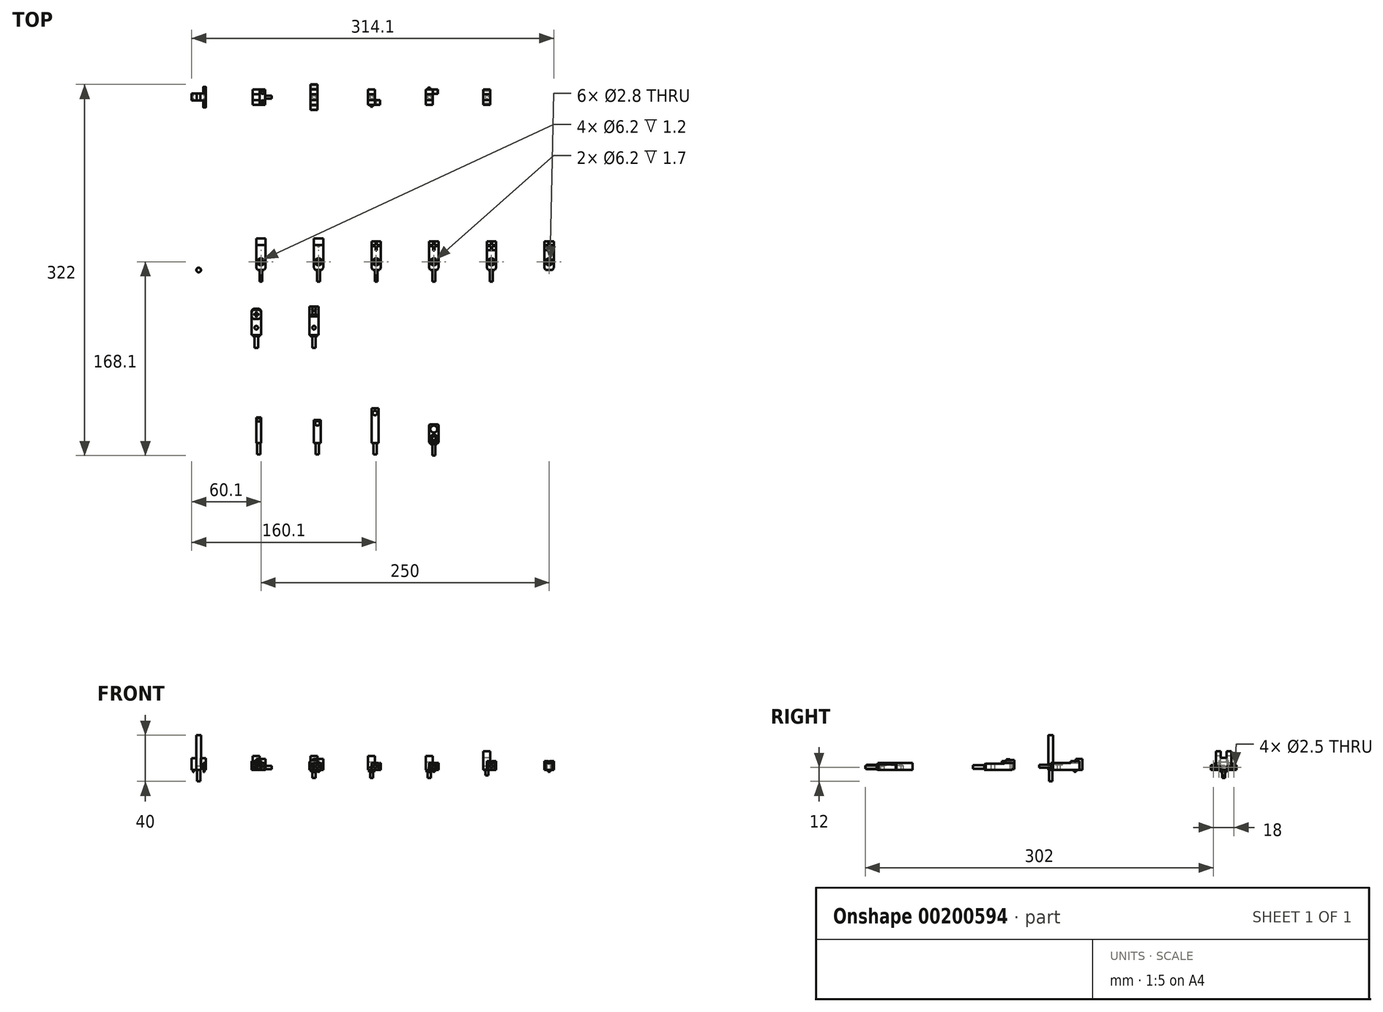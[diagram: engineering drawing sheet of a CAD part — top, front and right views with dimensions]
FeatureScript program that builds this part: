
annotation { "Feature Type Name" : "Feature", "Feature Type Description" : "" }
export const myFeature = defineFeature(function(context is Context, id is Id, definition is map)
    precondition{}
    {
        {
            var Q0;
            Q0=qCreatedBy(makeId("Top.planeOp"),FACE);
            var sketch = newSketch(context, id + "F0", { "sketchPlane" : qUnion([Q0])});
            skPoint(sketch, "E0", {"position": v(0, 0) * mm});
            skPoint(sketch, "E1.0.1.0", {"position": v(0, -50) * mm});
            skPoint(sketch, "E1.0.2.0", {"position": v(0, -100) * mm});
            skPoint(sketch, "E1.0.3.0", {"position": v(0, -150) * mm});
            skPoint(sketch, "E1.0.4.0", {"position": v(0, -200) * mm});
            skPoint(sketch, "E1.0.5.0", {"position": v(0, -250) * mm});
            skPoint(sketch, "E1.0.6.0", {"position": v(0, -300) * mm});
            skPoint(sketch, "E1.0.7.0", {"position": v(0, -350) * mm});
            skPoint(sketch, "E1.0.8.0", {"position": v(0, -400) * mm});
            skPoint(sketch, "E1.0.9.0", {"position": v(0, -450) * mm});
            skPoint(sketch, "E1.1.0.0", {"position": v(50, 0) * mm});
            skPoint(sketch, "E1.1.1.0", {"position": v(50, -50) * mm});
            skPoint(sketch, "E1.1.2.0", {"position": v(50, -100) * mm});
            skPoint(sketch, "E1.1.3.0", {"position": v(50, -150) * mm});
            skPoint(sketch, "E1.1.4.0", {"position": v(50, -200) * mm});
            skPoint(sketch, "E1.1.5.0", {"position": v(50, -250) * mm});
            skPoint(sketch, "E1.1.6.0", {"position": v(50, -300) * mm});
            skPoint(sketch, "E1.1.7.0", {"position": v(50, -350) * mm});
            skPoint(sketch, "E1.1.8.0", {"position": v(50, -400) * mm});
            skPoint(sketch, "E1.1.9.0", {"position": v(50, -450) * mm});
            skPoint(sketch, "E1.2.0.0", {"position": v(100, 0) * mm});
            skPoint(sketch, "E1.2.1.0", {"position": v(100, -50) * mm});
            skPoint(sketch, "E1.2.2.0", {"position": v(100, -100) * mm});
            skPoint(sketch, "E1.2.3.0", {"position": v(100, -150) * mm});
            skPoint(sketch, "E1.2.4.0", {"position": v(100, -200) * mm});
            skPoint(sketch, "E1.2.5.0", {"position": v(100, -250) * mm});
            skPoint(sketch, "E1.2.6.0", {"position": v(100, -300) * mm});
            skPoint(sketch, "E1.2.7.0", {"position": v(100, -350) * mm});
            skPoint(sketch, "E1.2.8.0", {"position": v(100, -400) * mm});
            skPoint(sketch, "E1.2.9.0", {"position": v(100, -450) * mm});
            skPoint(sketch, "E1.3.0.0", {"position": v(150, 0) * mm});
            skPoint(sketch, "E1.3.1.0", {"position": v(150, -50) * mm});
            skPoint(sketch, "E1.3.2.0", {"position": v(150, -100) * mm});
            skPoint(sketch, "E1.3.3.0", {"position": v(150, -150) * mm});
            skPoint(sketch, "E1.3.4.0", {"position": v(150, -200) * mm});
            skPoint(sketch, "E1.3.5.0", {"position": v(150, -250) * mm});
            skPoint(sketch, "E1.3.6.0", {"position": v(150, -300) * mm});
            skPoint(sketch, "E1.3.7.0", {"position": v(150, -350) * mm});
            skPoint(sketch, "E1.3.8.0", {"position": v(150, -400) * mm});
            skPoint(sketch, "E1.3.9.0", {"position": v(150, -450) * mm});
            skPoint(sketch, "E1.4.0.0", {"position": v(200, 0) * mm});
            skPoint(sketch, "E1.4.1.0", {"position": v(200, -50) * mm});
            skPoint(sketch, "E1.4.2.0", {"position": v(200, -100) * mm});
            skPoint(sketch, "E1.4.3.0", {"position": v(200, -150) * mm});
            skPoint(sketch, "E1.4.4.0", {"position": v(200, -200) * mm});
            skPoint(sketch, "E1.4.5.0", {"position": v(200, -250) * mm});
            skPoint(sketch, "E1.4.6.0", {"position": v(200, -300) * mm});
            skPoint(sketch, "E1.4.7.0", {"position": v(200, -350) * mm});
            skPoint(sketch, "E1.4.8.0", {"position": v(200, -400) * mm});
            skPoint(sketch, "E1.4.9.0", {"position": v(200, -450) * mm});
            skPoint(sketch, "E1.5.0.0", {"position": v(250, 0) * mm});
            skPoint(sketch, "E1.5.1.0", {"position": v(250, -50) * mm});
            skPoint(sketch, "E1.5.2.0", {"position": v(250, -100) * mm});
            skPoint(sketch, "E1.5.3.0", {"position": v(250, -150) * mm});
            skPoint(sketch, "E1.5.4.0", {"position": v(250, -200) * mm});
            skPoint(sketch, "E1.5.5.0", {"position": v(250, -250) * mm});
            skPoint(sketch, "E1.5.6.0", {"position": v(250, -300) * mm});
            skPoint(sketch, "E1.5.7.0", {"position": v(250, -350) * mm});
            skPoint(sketch, "E1.5.8.0", {"position": v(250, -400) * mm});
            skPoint(sketch, "E1.5.9.0", {"position": v(250, -450) * mm});
            skPoint(sketch, "E1.6.0.0", {"position": v(300, 0) * mm});
            skPoint(sketch, "E1.6.1.0", {"position": v(300, -50) * mm});
            skPoint(sketch, "E1.6.2.0", {"position": v(300, -100) * mm});
            skPoint(sketch, "E1.6.3.0", {"position": v(300, -150) * mm});
            skPoint(sketch, "E1.6.4.0", {"position": v(300, -200) * mm});
            skPoint(sketch, "E1.6.5.0", {"position": v(300, -250) * mm});
            skPoint(sketch, "E1.6.6.0", {"position": v(300, -300) * mm});
            skPoint(sketch, "E1.6.7.0", {"position": v(300, -350) * mm});
            skPoint(sketch, "E1.6.8.0", {"position": v(300, -400) * mm});
            skPoint(sketch, "E1.6.9.0", {"position": v(300, -450) * mm});
            skPoint(sketch, "E1.7.0.0", {"position": v(350, 0) * mm});
            skPoint(sketch, "E1.7.1.0", {"position": v(350, -50) * mm});
            skPoint(sketch, "E1.7.2.0", {"position": v(350, -100) * mm});
            skPoint(sketch, "E1.7.3.0", {"position": v(350, -150) * mm});
            skPoint(sketch, "E1.7.4.0", {"position": v(350, -200) * mm});
            skPoint(sketch, "E1.7.5.0", {"position": v(350, -250) * mm});
            skPoint(sketch, "E1.7.6.0", {"position": v(350, -300) * mm});
            skPoint(sketch, "E1.7.7.0", {"position": v(350, -350) * mm});
            skPoint(sketch, "E1.7.8.0", {"position": v(350, -400) * mm});
            skPoint(sketch, "E1.7.9.0", {"position": v(350, -450) * mm});
            skPoint(sketch, "E1.8.0.0", {"position": v(400, 0) * mm});
            skPoint(sketch, "E1.8.1.0", {"position": v(400, -50) * mm});
            skPoint(sketch, "E1.8.2.0", {"position": v(400, -100) * mm});
            skPoint(sketch, "E1.8.3.0", {"position": v(400, -150) * mm});
            skPoint(sketch, "E1.8.4.0", {"position": v(400, -200) * mm});
            skPoint(sketch, "E1.8.5.0", {"position": v(400, -250) * mm});
            skPoint(sketch, "E1.8.6.0", {"position": v(400, -300) * mm});
            skPoint(sketch, "E1.8.7.0", {"position": v(400, -350) * mm});
            skPoint(sketch, "E1.8.8.0", {"position": v(400, -400) * mm});
            skPoint(sketch, "E1.8.9.0", {"position": v(400, -450) * mm});
            skPoint(sketch, "E1.9.0.0", {"position": v(450, 0) * mm});
            skPoint(sketch, "E1.9.1.0", {"position": v(450, -50) * mm});
            skPoint(sketch, "E1.9.2.0", {"position": v(450, -100) * mm});
            skPoint(sketch, "E1.9.3.0", {"position": v(450, -150) * mm});
            skPoint(sketch, "E1.9.4.0", {"position": v(450, -200) * mm});
            skPoint(sketch, "E1.9.5.0", {"position": v(450, -250) * mm});
            skPoint(sketch, "E1.9.6.0", {"position": v(450, -300) * mm});
            skPoint(sketch, "E1.9.7.0", {"position": v(450, -350) * mm});
            skPoint(sketch, "E1.9.8.0", {"position": v(450, -400) * mm});
            skPoint(sketch, "E1.9.9.0", {"position": v(450, -450) * mm});
            skLineSegment(sketch, "E1.direction1", {"start": v(0, 0) * mm, "end": v(50, 0) * mm, "construction": true});
            skLineSegment(sketch, "E1.direction2", {"start": v(0, 0) * mm, "end": v(0, -50) * mm, "construction": true});
            skSolve(sketch);
        }
        {
            var Q0;
            Q0=qCreatedBy(makeId("Top.planeOp"),FACE);
            var sketch = newSketch(context, id + "F1", { "sketchPlane" : qUnion([Q0])});
            skLineSegment(sketch, "E2.bottom", {"start": v(6.1, 3) * mm, "end": v(-6.1, 3) * mm});
            skLineSegment(sketch, "E2.top", {"start": v(6.1, -3) * mm, "end": v(-6.1, -3) * mm});
            skLineSegment(sketch, "E2.left", {"start": v(6.1, 3) * mm, "end": v(6.1, -3) * mm});
            skLineSegment(sketch, "E2.right", {"start": v(-6.1, 3) * mm, "end": v(-6.1, -3) * mm});
            skPoint(sketch, "E2.middle", {"position": v(0, 0) * mm});
            skSolve(sketch);
        }
        {
            var Q0;
            Q0 = qSketchRegion(id + "F1", true);
            extrude(context, id + "F2", {"entities" : qUnion([Q0]), "depth" : 10 * mm});
        }
        {
            var Q0;
            Q0=makeQuery(id+"F2.opExtrude","SWEPT_FACE",FACE,{"disambiguationData":[OSD([sQuery(id+"F1.wireOp",EDGE,"E2.left")])]});
            var sketch = newSketch(context, id + "F3", { "sketchPlane" : qUnion([Q0])});
            skLineSegment(sketch, "E3.bottom", {"start": v(6, 6) * mm, "end": v(-6, 6) * mm});
            skLineSegment(sketch, "E3.top", {"start": v(6, 0) * mm, "end": v(-6, 0) * mm});
            skPoint(sketch, "E3.middle", {"position": v(0, 3) * mm});
            skPoint(sketch, "E3.middle.positionSnap0", {"position": v(0, 0) * mm});
            skPoint(sketch, "E3.centerSnap0", {"position": v(0, 0) * mm});
            skArc(sketch, "E4", {"start": v(-6, 6) * mm, "mid": v(-9, 3) * mm, "end": v(-6, 0) * mm});
            skArc(sketch, "E5", {"start": v(6, 0) * mm, "mid": v(9, 3) * mm, "end": v(6, 6) * mm});
            skSolve(sketch);
        }
        {
            var Q0;
            Q0 = qSketchRegion(id + "F3", true);
            extrude(context, id + "F4", {"entities" : qUnion([Q0]), "operationType" : NewBodyOperationType.ADD, "oppositeDirection" : true, "depth" : 2 * mm});
        }
        {
            var Q0;
            Q0=makeQuery(id+"F4.boolean.opBoolean","MERGE",FACE,{"derivedFrom":[makeQuery(id+"F2.opExtrude","SWEPT_FACE",FACE,{"disambiguationData":[OSD([sQuery(id+"F1.wireOp",EDGE,"E2.left")])]}),makeQuery(id+"F4.opExtrude","CAP_FACE",FACE,{"disambiguationData":[OSD([sQuery(id+"F3.wireOp",EDGE,"E3.bottom"),sQuery(id+"F3.wireOp",EDGE,"E3.top"),sQuery(id+"F3.wireOp",EDGE,"E4"),sQuery(id+"F3.wireOp",EDGE,"E5")])],"isStart":true})]});
            var sketch = newSketch(context, id + "F5", { "sketchPlane" : qUnion([Q0])});
            skCircle(sketch, "E6", {"center": v(-6, 3) * mm, "radius": 1.6 * mm});
            skCircle(sketch, "E7", {"center": v(6, 3) * mm, "radius": 1.6 * mm});
            skSolve(sketch);
        }
        {
            var Q0;
            Q0 = qSketchRegion(id + "F5", true);
            extrude(context, id + "F6", {"entities" : qUnion([Q0]), "operationType" : NewBodyOperationType.REMOVE, "endBound" : BoundingType.UP_TO_NEXT, "oppositeDirection" : true, "depth" : 25 * mm});
        }
        {
            var Q0;
            Q0=makeQuery(id+"F2.opExtrude","CAP_FACE",FACE,{"disambiguationData":[OSD([sQuery(id+"F1.wireOp",EDGE,"E2.bottom"),sQuery(id+"F1.wireOp",EDGE,"E2.top"),sQuery(id+"F1.wireOp",EDGE,"E2.left"),sQuery(id+"F1.wireOp",EDGE,"E2.right")])],"isStart":false});
            var sketch = newSketch(context, id + "F7", { "sketchPlane" : qUnion([Q0])});
            skLineSegment(sketch, "E8.bottom", {"start": v(1.6, 3) * mm, "end": v(-1.6, 3) * mm});
            skLineSegment(sketch, "E8.top", {"start": v(1.6, -3) * mm, "end": v(-1.6, -3) * mm});
            skLineSegment(sketch, "E8.left", {"start": v(1.6, 3) * mm, "end": v(1.6, -3) * mm});
            skLineSegment(sketch, "E8.right", {"start": v(-1.6, 3) * mm, "end": v(-1.6, -3) * mm});
            skPoint(sketch, "E8.middle", {"position": v(0, 0) * mm});
            skSolve(sketch);
        }
        {
            var Q0;
            Q0 = qSketchRegion(id + "F7", true);
            extrude(context, id + "F8", {"entities" : qUnion([Q0]), "operationType" : NewBodyOperationType.REMOVE, "oppositeDirection" : true, "depth" : 7 * mm});
        }
        {
            var Q0;
            Q0=makeQuery(id+"F4.boolean.opBoolean","MERGE",FACE,{"derivedFrom":[makeQuery(id+"F2.opExtrude","CAP_FACE",FACE,{"disambiguationData":[OSD([sQuery(id+"F1.wireOp",EDGE,"E2.bottom"),sQuery(id+"F1.wireOp",EDGE,"E2.top"),sQuery(id+"F1.wireOp",EDGE,"E2.left"),sQuery(id+"F1.wireOp",EDGE,"E2.right")])],"isStart":true}),makeQuery(id+"F4.opExtrude","SWEPT_FACE",FACE,{"disambiguationData":[OSD([sQuery(id+"F3.wireOp",EDGE,"E3.top")])]})]});
            var sketch = newSketch(context, id + "F9", { "sketchPlane" : qUnion([Q0])});
            skLineSegment(sketch, "E9.bottom", {"start": v(4.6, 1.27) * mm, "end": v(-4.6, 1.27) * mm, "construction": true});
            skLineSegment(sketch, "E9.top", {"start": v(4.6, -1.27) * mm, "end": v(-4.6, -1.27) * mm, "construction": true});
            skLineSegment(sketch, "E9.left", {"start": v(4.6, 1.27) * mm, "end": v(4.6, -1.27) * mm, "construction": true});
            skLineSegment(sketch, "E9.right", {"start": v(-4.6, 1.27) * mm, "end": v(-4.6, -1.27) * mm, "construction": true});
            skPoint(sketch, "E9.middle", {"position": v(0, 0) * mm});
            skCircle(sketch, "E10", {"center": v(-4.6, 1.27) * mm, "radius": 0.23 * mm});
            skCircle(sketch, "E11", {"center": v(4.6, 1.27) * mm, "radius": 0.23 * mm});
            skCircle(sketch, "E12", {"center": v(4.6, -1.27) * mm, "radius": 0.23 * mm});
            skCircle(sketch, "E13", {"center": v(-4.6, -1.27) * mm, "radius": 0.23 * mm});
            skSolve(sketch);
        }
        {
            var Q0;
            Q0 = qSketchRegion(id + "F9", true);
            extrude(context, id + "F10", {"entities" : qUnion([Q0]), "operationType" : NewBodyOperationType.ADD, "depth" : 2 * mm});
        }
        {
            var Q0;
            Q0=qCreatedBy(makeId("Top.planeOp"),FACE);
            var sketch = newSketch(context, id + "F11", { "sketchPlane" : qUnion([Q0])});
            skLineSegment(sketch, "E14.bottom", {"start": v(53, 6.7) * mm, "end": v(47, 6.7) * mm});
            skLineSegment(sketch, "E14.top", {"start": v(53, -6.7) * mm, "end": v(47, -6.7) * mm});
            skLineSegment(sketch, "E14.left", {"start": v(53, 6.7) * mm, "end": v(53, -6.7) * mm});
            skLineSegment(sketch, "E14.right", {"start": v(47, 6.7) * mm, "end": v(47, -6.7) * mm});
            skPoint(sketch, "E14.middle", {"position": v(50, 0) * mm});
            skSolve(sketch);
        }
        {
            var Q0;
            Q0 = qSketchRegion(id + "F11", true);
            extrude(context, id + "F12", {"entities" : qUnion([Q0]), "depth" : 12 * mm});
        }
        {
            var Q0;
            Q0=makeQuery(id+"F12.opExtrude","CAP_FACE",FACE,{"disambiguationData":[OSD([sQuery(id+"F11.wireOp",EDGE,"E14.bottom"),sQuery(id+"F11.wireOp",EDGE,"E14.top"),sQuery(id+"F11.wireOp",EDGE,"E14.left"),sQuery(id+"F11.wireOp",EDGE,"E14.right")])],"isStart":false});
            var sketch = newSketch(context, id + "F13", { "sketchPlane" : qUnion([Q0])});
            skLineSegment(sketch, "E15.bottom", {"start": v(53, 2.5) * mm, "end": v(47, 2.5) * mm});
            skLineSegment(sketch, "E15.top", {"start": v(53, -2.5) * mm, "end": v(47, -2.5) * mm});
            skLineSegment(sketch, "E15.left", {"start": v(53, 2.5) * mm, "end": v(53, -2.5) * mm});
            skLineSegment(sketch, "E15.right", {"start": v(47, 2.5) * mm, "end": v(47, -2.5) * mm});
            skPoint(sketch, "E15.middle", {"position": v(50, 0) * mm});
            skPoint(sketch, "E15.middle.positionSnap0", {"position": v(50, 6.7) * mm});
            skPoint(sketch, "E15.middle.positionSnap1", {"position": v(47, 0) * mm});
            skPoint(sketch, "E15.centerSnap0", {"position": v(50, 6.7) * mm});
            skPoint(sketch, "E15.centerSnap1", {"position": v(47, 0) * mm});
            skSolve(sketch);
        }
        {
            var Q0;
            Q0 = qSketchRegion(id + "F13", true);
            extrude(context, id + "F14", {"entities" : qUnion([Q0]), "operationType" : NewBodyOperationType.REMOVE, "oppositeDirection" : true, "depth" : 5.5 * mm});
        }
        {
            var Q0;
            Q0=makeQuery(id+"F12.opExtrude","SWEPT_FACE",FACE,{"disambiguationData":[OSD([sQuery(id+"F11.wireOp",EDGE,"E14.left")])]});
            var sketch = newSketch(context, id + "F15", { "sketchPlane" : qUnion([Q0])});
            skLineSegment(sketch, "E16.bottom", {"start": v(-6.7, 0) * mm, "end": v(6.7, 0) * mm});
            skLineSegment(sketch, "E16.top", {"start": v(-6.7, 4) * mm, "end": v(6.7, 4) * mm});
            skLineSegment(sketch, "E16.left", {"start": v(-6.7, 0) * mm, "end": v(-6.7, 4) * mm});
            skLineSegment(sketch, "E16.right", {"start": v(6.7, 0) * mm, "end": v(6.7, 4) * mm});
            skSolve(sketch);
        }
        {
            var Q0;
            Q0 = qSketchRegion(id + "F15", true);
            extrude(context, id + "F16", {"entities" : qUnion([Q0]), "operationType" : NewBodyOperationType.ADD, "depth" : 4.5 * mm});
        }
        {
            var Q0;
            Q0=makeQuery(id+"F16.opExtrude","SWEPT_FACE",FACE,{"disambiguationData":[OSD([sQuery(id+"F15.wireOp",EDGE,"E16.top")])]});
            var sketch = newSketch(context, id + "F17", { "sketchPlane" : qUnion([Q0])});
            skCircle(sketch, "E17", {"center": v(55.5, -4) * mm, "radius": 1.25 * mm});
            skCircle(sketch, "E18", {"center": v(55.5, 4) * mm, "radius": 1.25 * mm});
            skLineSegment(sketch, "E19", {"start": v(53, 0) * mm, "end": v(57.5, 0) * mm, "construction": true});
            skSolve(sketch);
        }
        {
            var Q0;
            Q0 = qSketchRegion(id + "F17", true);
            extrude(context, id + "F18", {"entities" : qUnion([Q0]), "operationType" : NewBodyOperationType.REMOVE, "endBound" : BoundingType.UP_TO_NEXT, "oppositeDirection" : true, "depth" : 25 * mm});
        }
        {
            var Q0;
            Q0=makeQuery(id+"F16.opExtrude","CAP_FACE",FACE,{"disambiguationData":[OSD([sQuery(id+"F15.wireOp",EDGE,"E16.bottom"),sQuery(id+"F15.wireOp",EDGE,"E16.top"),sQuery(id+"F15.wireOp",EDGE,"E16.left"),sQuery(id+"F15.wireOp",EDGE,"E16.right")])],"isStart":false});
            var sketch = newSketch(context, id + "F19", { "sketchPlane" : qUnion([Q0])});
            skCircle(sketch, "E20", {"center": v(0, 2) * mm, "radius": 1.35 * mm});
            skPoint(sketch, "E20.centerSnap0", {"position": v(0, 0) * mm});
            skSolve(sketch);
        }
        {
            var Q0;
            Q0 = qSketchRegion(id + "F19", true);
            extrude(context, id + "F20", {"entities" : qUnion([Q0]), "operationType" : NewBodyOperationType.ADD, "depth" : 6 * mm});
        }
        {
            var Q0;
            Q0=qCreatedBy(makeId("Top.planeOp"),FACE);
            var sketch = newSketch(context, id + "F21", { "sketchPlane" : qUnion([Q0])});
            skLineSegment(sketch, "E21.bottom", {"start": v(103, 11) * mm, "end": v(97, 11) * mm});
            skLineSegment(sketch, "E21.top", {"start": v(103, -11) * mm, "end": v(97, -11) * mm});
            skLineSegment(sketch, "E21.left", {"start": v(103, 11) * mm, "end": v(103, -11) * mm});
            skLineSegment(sketch, "E21.right", {"start": v(97, 11) * mm, "end": v(97, -11) * mm});
            skPoint(sketch, "E21.middle", {"position": v(100, 0) * mm});
            skSolve(sketch);
        }
        {
            var Q0;
            Q0 = qSketchRegion(id + "F21", true);
            extrude(context, id + "F22", {"entities" : qUnion([Q0]), "depth" : 4 * mm});
        }
        {
            var Q0;
            Q0=makeQuery(id+"F22.opExtrude","CAP_FACE",FACE,{"disambiguationData":[OSD([sQuery(id+"F21.wireOp",EDGE,"E21.bottom"),sQuery(id+"F21.wireOp",EDGE,"E21.top"),sQuery(id+"F21.wireOp",EDGE,"E21.left"),sQuery(id+"F21.wireOp",EDGE,"E21.right")])],"isStart":false});
            var sketch = newSketch(context, id + "F23", { "sketchPlane" : qUnion([Q0])});
            skLineSegment(sketch, "E22.bottom", {"start": v(103, 6.7) * mm, "end": v(97, 6.7) * mm});
            skLineSegment(sketch, "E22.top", {"start": v(103, -6.7) * mm, "end": v(97, -6.7) * mm});
            skLineSegment(sketch, "E22.left", {"start": v(103, 6.7) * mm, "end": v(103, -6.7) * mm});
            skLineSegment(sketch, "E22.right", {"start": v(97, 6.7) * mm, "end": v(97, -6.7) * mm});
            skPoint(sketch, "E22.middle", {"position": v(100, 0) * mm});
            skPoint(sketch, "E22.middle.positionSnap0", {"position": v(100, -11) * mm});
            skPoint(sketch, "E22.middle.positionSnap1", {"position": v(103, 0) * mm});
            skPoint(sketch, "E22.centerSnap0", {"position": v(100, -11) * mm});
            skPoint(sketch, "E22.centerSnap1", {"position": v(103, 0) * mm});
            skSolve(sketch);
        }
        {
            var Q0;
            Q0 = qSketchRegion(id + "F23", true);
            extrude(context, id + "F24", {"entities" : qUnion([Q0]), "operationType" : NewBodyOperationType.ADD, "depth" : 8 * mm});
        }
        {
            var Q0;
            Q0=makeQuery(id+"F24.opExtrude","CAP_FACE",FACE,{"disambiguationData":[OSD([sQuery(id+"F23.wireOp",EDGE,"E22.bottom"),sQuery(id+"F23.wireOp",EDGE,"E22.top"),sQuery(id+"F23.wireOp",EDGE,"E22.left"),sQuery(id+"F23.wireOp",EDGE,"E22.right")])],"isStart":false});
            var sketch = newSketch(context, id + "F25", { "sketchPlane" : qUnion([Q0])});
            skLineSegment(sketch, "E23.bottom", {"start": v(103, 2.5) * mm, "end": v(97, 2.5) * mm});
            skLineSegment(sketch, "E23.top", {"start": v(103, -2.5) * mm, "end": v(97, -2.5) * mm});
            skLineSegment(sketch, "E23.left", {"start": v(103, 2.5) * mm, "end": v(103, -2.5) * mm});
            skLineSegment(sketch, "E23.right", {"start": v(97, 2.5) * mm, "end": v(97, -2.5) * mm});
            skPoint(sketch, "E23.middle", {"position": v(100, 0) * mm});
            skPoint(sketch, "E23.middle.positionSnap0", {"position": v(100, 6.7) * mm});
            skPoint(sketch, "E23.middle.positionSnap1", {"position": v(97, 0) * mm});
            skPoint(sketch, "E23.centerSnap0", {"position": v(100, 6.7) * mm});
            skPoint(sketch, "E23.centerSnap1", {"position": v(97, 0) * mm});
            skSolve(sketch);
        }
        {
            var Q0;
            Q0 = qSketchRegion(id + "F25", true);
            extrude(context, id + "F26", {"entities" : qUnion([Q0]), "operationType" : NewBodyOperationType.REMOVE, "oppositeDirection" : true, "depth" : 5.5 * mm});
        }
        {
            var Q0;
            Q0=makeQuery(id+"F24.boolean.opBoolean","MERGE",FACE,{"derivedFrom":[makeQuery(id+"F22.opExtrude","SWEPT_FACE",FACE,{"disambiguationData":[OSD([sQuery(id+"F21.wireOp",EDGE,"E21.left")])]}),makeQuery(id+"F24.opExtrude","SWEPT_FACE",FACE,{"disambiguationData":[OSD([sQuery(id+"F23.wireOp",EDGE,"E22.left")])]})]});
            var sketch = newSketch(context, id + "F27", { "sketchPlane" : qUnion([Q0])});
            skCircle(sketch, "E24", {"center": v(-9, 2) * mm, "radius": 1.25 * mm});
            skCircle(sketch, "E25", {"center": v(9, 2) * mm, "radius": 1.25 * mm});
            skLineSegment(sketch, "E26", {"start": v(-11, 2) * mm, "end": v(11, 2) * mm, "construction": true});
            skSolve(sketch);
        }
        {
            var Q0;
            Q0 = qSketchRegion(id + "F27", true);
            extrude(context, id + "F28", {"entities" : qUnion([Q0]), "operationType" : NewBodyOperationType.REMOVE, "endBound" : BoundingType.UP_TO_NEXT, "oppositeDirection" : true, "depth" : 25 * mm});
        }
        {
            var Q0;
            Q0=makeQuery(id+"F22.opExtrude","CAP_FACE",FACE,{"disambiguationData":[OSD([sQuery(id+"F21.wireOp",EDGE,"E21.bottom"),sQuery(id+"F21.wireOp",EDGE,"E21.top"),sQuery(id+"F21.wireOp",EDGE,"E21.left"),sQuery(id+"F21.wireOp",EDGE,"E21.right")])],"isStart":true});
            var sketch = newSketch(context, id + "F29", { "sketchPlane" : qUnion([Q0])});
            skCircle(sketch, "E27", {"center": v(100, 0) * mm, "radius": 2.4 * mm});
            skPoint(sketch, "E27.centerSnap0", {"position": v(100, 11) * mm});
            skPoint(sketch, "E27.centerSnap1", {"position": v(103, 0) * mm});
            skSolve(sketch);
        }
        {
            var Q0;
            Q0 = qSketchRegion(id + "F29", true);
            extrude(context, id + "F30", {"entities" : qUnion([Q0]), "operationType" : NewBodyOperationType.ADD, "depth" : 2 * mm});
        }
        {
            var Q0;
            Q0=makeQuery(id+"F30.opExtrude","CAP_FACE",FACE,{"disambiguationData":[OSD([sQuery(id+"F29.wireOp",EDGE,"E27")])],"isStart":false});
            var sketch = newSketch(context, id + "F31", { "sketchPlane" : qUnion([Q0])});
            skCircle(sketch, "E28", {"center": v(100, 0) * mm, "radius": 1.35 * mm});
            skSolve(sketch);
        }
        {
            var Q0;
            Q0 = qSketchRegion(id + "F31", true);
            extrude(context, id + "F32", {"entities" : qUnion([Q0]), "operationType" : NewBodyOperationType.ADD, "depth" : 5 * mm});
        }
        {
            var Q0;
            Q0=qCreatedBy(makeId("Top.planeOp"),FACE);
            var sketch = newSketch(context, id + "F33", { "sketchPlane" : qUnion([Q0])});
            skLineSegment(sketch, "E29.bottom", {"start": v(153, 6.7) * mm, "end": v(147, 6.7) * mm});
            skLineSegment(sketch, "E29.top", {"start": v(153, -6.7) * mm, "end": v(147, -6.7) * mm});
            skLineSegment(sketch, "E29.left", {"start": v(153, 6.7) * mm, "end": v(153, -6.7) * mm});
            skLineSegment(sketch, "E29.right", {"start": v(147, 6.7) * mm, "end": v(147, -6.7) * mm});
            skPoint(sketch, "E29.middle", {"position": v(150, 0) * mm});
            skSolve(sketch);
        }
        {
            var Q0;
            Q0 = qSketchRegion(id + "F33", true);
            extrude(context, id + "F34", {"entities" : qUnion([Q0]), "depth" : 12 * mm});
        }
        {
            var Q0;
            Q0=makeQuery(id+"F34.opExtrude","CAP_FACE",FACE,{"disambiguationData":[OSD([sQuery(id+"F33.wireOp",EDGE,"E29.bottom"),sQuery(id+"F33.wireOp",EDGE,"E29.top"),sQuery(id+"F33.wireOp",EDGE,"E29.left"),sQuery(id+"F33.wireOp",EDGE,"E29.right")])],"isStart":false});
            var sketch = newSketch(context, id + "F35", { "sketchPlane" : qUnion([Q0])});
            skLineSegment(sketch, "E30.bottom", {"start": v(153, 2.5) * mm, "end": v(147, 2.5) * mm});
            skLineSegment(sketch, "E30.top", {"start": v(153, -2.5) * mm, "end": v(147, -2.5) * mm});
            skLineSegment(sketch, "E30.left", {"start": v(153, 2.5) * mm, "end": v(153, -2.5) * mm});
            skLineSegment(sketch, "E30.right", {"start": v(147, 2.5) * mm, "end": v(147, -2.5) * mm});
            skPoint(sketch, "E30.middle", {"position": v(150, 0) * mm});
            skPoint(sketch, "E30.middle.positionSnap0", {"position": v(147, 0) * mm});
            skPoint(sketch, "E30.middle.positionSnap1", {"position": v(150, 6.7) * mm});
            skPoint(sketch, "E30.centerSnap0", {"position": v(147, 0) * mm});
            skPoint(sketch, "E30.centerSnap1", {"position": v(150, 6.7) * mm});
            skSolve(sketch);
        }
        {
            var Q0;
            Q0 = qSketchRegion(id + "F35", true);
            extrude(context, id + "F36", {"entities" : qUnion([Q0]), "operationType" : NewBodyOperationType.REMOVE, "oppositeDirection" : true, "depth" : 5.5 * mm});
        }
        {
            var Q0;
            Q0=makeQuery(id+"F34.opExtrude","SWEPT_FACE",FACE,{"disambiguationData":[OSD([sQuery(id+"F33.wireOp",EDGE,"E29.left")])]});
            var sketch = newSketch(context, id + "F37", { "sketchPlane" : qUnion([Q0])});
            skLineSegment(sketch, "E31.bottom", {"start": v(-6.7, 0) * mm, "end": v(-2.7, 0) * mm});
            skLineSegment(sketch, "E31.top", {"start": v(-6.7, 4) * mm, "end": v(-2.7, 4) * mm});
            skLineSegment(sketch, "E31.left", {"start": v(-6.7, 0) * mm, "end": v(-6.7, 4) * mm});
            skLineSegment(sketch, "E31.right", {"start": v(-2.7, 0) * mm, "end": v(-2.7, 4) * mm});
            skSolve(sketch);
        }
        {
            var Q0;
            Q0 = qSketchRegion(id + "F37", true);
            extrude(context, id + "F38", {"entities" : qUnion([Q0]), "operationType" : NewBodyOperationType.ADD, "depth" : 4.5 * mm});
        }
        {
            var Q0;
            Q0=makeQuery(id+"F38.boolean.opBoolean","MERGE",FACE,{"derivedFrom":[makeQuery(id+"F34.opExtrude","SWEPT_FACE",FACE,{"disambiguationData":[OSD([sQuery(id+"F33.wireOp",EDGE,"E29.top")])]}),makeQuery(id+"F38.opExtrude","SWEPT_FACE",FACE,{"disambiguationData":[OSD([sQuery(id+"F37.wireOp",EDGE,"E31.left")])]})]});
            var sketch = newSketch(context, id + "F39", { "sketchPlane" : qUnion([Q0])});
            skCircle(sketch, "E32", {"center": v(155.5, 2) * mm, "radius": 1.25 * mm});
            skPoint(sketch, "E32.centerSnap0", {"position": v(157.5, 2) * mm});
            skSolve(sketch);
        }
        {
            var Q0;
            Q0 = qSketchRegion(id + "F39", true);
            extrude(context, id + "F40", {"entities" : qUnion([Q0]), "operationType" : NewBodyOperationType.REMOVE, "endBound" : BoundingType.UP_TO_NEXT, "oppositeDirection" : true, "depth" : 25 * mm});
        }
        {
            var Q0;
            Q0=makeQuery(id+"F38.boolean.opBoolean","MERGE",FACE,{"derivedFrom":[makeQuery(id+"F34.opExtrude","SWEPT_FACE",FACE,{"disambiguationData":[OSD([sQuery(id+"F33.wireOp",EDGE,"E29.top")])]}),makeQuery(id+"F38.opExtrude","SWEPT_FACE",FACE,{"disambiguationData":[OSD([sQuery(id+"F37.wireOp",EDGE,"E31.left")])]})]});
            var sketch = newSketch(context, id + "F41", { "sketchPlane" : qUnion([Q0])});
            skCircle(sketch, "E33", {"center": v(150, 2) * mm, "radius": 1 * mm});
            skPoint(sketch, "E33.centerSnap0", {"position": v(157.5, 2) * mm});
            skPoint(sketch, "E33.centerSnap1", {"position": v(150, 12) * mm});
            skSolve(sketch);
        }
        {
            var Q0;
            Q0 = qSketchRegion(id + "F41", true);
            extrude(context, id + "F42", {"entities" : qUnion([Q0]), "operationType" : NewBodyOperationType.ADD, "depth" : 1.5 * mm});
        }
        {
            var Q0;
            Q0=makeQuery(id+"F38.boolean.opBoolean","MERGE",FACE,{"derivedFrom":[makeQuery(id+"F34.opExtrude","CAP_FACE",FACE,{"disambiguationData":[OSD([sQuery(id+"F33.wireOp",EDGE,"E29.bottom"),sQuery(id+"F33.wireOp",EDGE,"E29.top"),sQuery(id+"F33.wireOp",EDGE,"E29.left"),sQuery(id+"F33.wireOp",EDGE,"E29.right")])],"isStart":true}),makeQuery(id+"F38.opExtrude","SWEPT_FACE",FACE,{"disambiguationData":[OSD([sQuery(id+"F37.wireOp",EDGE,"E31.bottom")])]})]});
            var sketch = newSketch(context, id + "F43", { "sketchPlane" : qUnion([Q0])});
            skCircle(sketch, "E34", {"center": v(150, 0) * mm, "radius": 2.25 * mm});
            skPoint(sketch, "E34.centerSnap0", {"position": v(150, -6.7) * mm});
            skPoint(sketch, "E34.centerSnap1", {"position": v(147, 0) * mm});
            skSolve(sketch);
        }
        {
            var Q0;
            Q0 = qSketchRegion(id + "F43", true);
            extrude(context, id + "F44", {"entities" : qUnion([Q0]), "operationType" : NewBodyOperationType.ADD, "depth" : 2 * mm});
        }
        {
            var Q0;
            Q0=makeQuery(id+"F44.opExtrude","CAP_FACE",FACE,{"disambiguationData":[OSD([sQuery(id+"F43.wireOp",EDGE,"E34")])],"isStart":false});
            var sketch = newSketch(context, id + "F45", { "sketchPlane" : qUnion([Q0])});
            skCircle(sketch, "E35", {"center": v(150, 0) * mm, "radius": 1.35 * mm});
            skSolve(sketch);
        }
        {
            var Q0;
            Q0 = qSketchRegion(id + "F45", true);
            extrude(context, id + "F46", {"entities" : qUnion([Q0]), "operationType" : NewBodyOperationType.ADD, "depth" : 5 * mm});
        }
        {
            var Q0;
            Q0=qCreatedBy(makeId("Top.planeOp"),FACE);
            var sketch = newSketch(context, id + "F47", { "sketchPlane" : qUnion([Q0])});
            skLineSegment(sketch, "E36.bottom", {"start": v(203, 6.7) * mm, "end": v(197, 6.7) * mm});
            skLineSegment(sketch, "E36.top", {"start": v(203, -6.7) * mm, "end": v(197, -6.7) * mm});
            skLineSegment(sketch, "E36.left", {"start": v(203, 6.7) * mm, "end": v(203, -6.7) * mm});
            skLineSegment(sketch, "E36.right", {"start": v(197, 6.7) * mm, "end": v(197, -6.7) * mm});
            skPoint(sketch, "E36.middle", {"position": v(200, 0) * mm});
            skSolve(sketch);
        }
        {
            var Q0;
            Q0 = qSketchRegion(id + "F47", true);
            extrude(context, id + "F48", {"entities" : qUnion([Q0]), "depth" : 12 * mm});
        }
        {
            var Q0;
            Q0=makeQuery(id+"F48.opExtrude","SWEPT_FACE",FACE,{"disambiguationData":[OSD([sQuery(id+"F47.wireOp",EDGE,"E36.left")])]});
            var sketch = newSketch(context, id + "F49", { "sketchPlane" : qUnion([Q0])});
            skLineSegment(sketch, "E37.bottom", {"start": v(6.7, 0) * mm, "end": v(2.7, 0) * mm});
            skLineSegment(sketch, "E37.top", {"start": v(6.7, 4) * mm, "end": v(2.7, 4) * mm});
            skLineSegment(sketch, "E37.left", {"start": v(6.7, 0) * mm, "end": v(6.7, 4) * mm});
            skLineSegment(sketch, "E37.right", {"start": v(2.7, 0) * mm, "end": v(2.7, 4) * mm});
            skSolve(sketch);
        }
        {
            var Q0;
            Q0 = qSketchRegion(id + "F49", true);
            extrude(context, id + "F50", {"entities" : qUnion([Q0]), "operationType" : NewBodyOperationType.ADD, "depth" : 4.5 * mm});
        }
        {
            var Q0;
            Q0=makeQuery(id+"F48.opExtrude","CAP_FACE",FACE,{"disambiguationData":[OSD([sQuery(id+"F47.wireOp",EDGE,"E36.bottom"),sQuery(id+"F47.wireOp",EDGE,"E36.top"),sQuery(id+"F47.wireOp",EDGE,"E36.left"),sQuery(id+"F47.wireOp",EDGE,"E36.right")])],"isStart":false});
            var sketch = newSketch(context, id + "F51", { "sketchPlane" : qUnion([Q0])});
            skLineSegment(sketch, "E38.bottom", {"start": v(203, 2.5) * mm, "end": v(197, 2.5) * mm});
            skLineSegment(sketch, "E38.top", {"start": v(203, -2.5) * mm, "end": v(197, -2.5) * mm});
            skLineSegment(sketch, "E38.left", {"start": v(203, 2.5) * mm, "end": v(203, -2.5) * mm});
            skLineSegment(sketch, "E38.right", {"start": v(197, 2.5) * mm, "end": v(197, -2.5) * mm});
            skPoint(sketch, "E38.middle", {"position": v(200, 0) * mm});
            skPoint(sketch, "E38.middle.positionSnap0", {"position": v(200, 6.7) * mm});
            skPoint(sketch, "E38.middle.positionSnap1", {"position": v(197, 0) * mm});
            skPoint(sketch, "E38.centerSnap0", {"position": v(200, 6.7) * mm});
            skPoint(sketch, "E38.centerSnap1", {"position": v(197, 0) * mm});
            skSolve(sketch);
        }
        {
            var Q0;
            Q0 = qSketchRegion(id + "F51", true);
            extrude(context, id + "F52", {"entities" : qUnion([Q0]), "operationType" : NewBodyOperationType.REMOVE, "oppositeDirection" : true, "depth" : 5.5 * mm});
        }
        {
            var Q0;
            Q0=makeQuery(id+"F50.boolean.opBoolean","MERGE",FACE,{"derivedFrom":[makeQuery(id+"F48.opExtrude","SWEPT_FACE",FACE,{"disambiguationData":[OSD([sQuery(id+"F47.wireOp",EDGE,"E36.bottom")])]}),makeQuery(id+"F50.opExtrude","SWEPT_FACE",FACE,{"disambiguationData":[OSD([sQuery(id+"F49.wireOp",EDGE,"E37.left")])]})]});
            var sketch = newSketch(context, id + "F53", { "sketchPlane" : qUnion([Q0])});
            skCircle(sketch, "E39", {"center": v(-205.5, 2) * mm, "radius": 1.35 * mm});
            skPoint(sketch, "E39.centerSnap0", {"position": v(-207.5, 2) * mm});
            skSolve(sketch);
        }
        {
            var Q0;
            Q0 = qSketchRegion(id + "F53", true);
            extrude(context, id + "F54", {"entities" : qUnion([Q0]), "operationType" : NewBodyOperationType.REMOVE, "endBound" : BoundingType.UP_TO_NEXT, "oppositeDirection" : true, "depth" : 25 * mm});
        }
        {
            var Q0;
            Q0=makeQuery(id+"F50.boolean.opBoolean","MERGE",FACE,{"derivedFrom":[makeQuery(id+"F48.opExtrude","SWEPT_FACE",FACE,{"disambiguationData":[OSD([sQuery(id+"F47.wireOp",EDGE,"E36.bottom")])]}),makeQuery(id+"F50.opExtrude","SWEPT_FACE",FACE,{"disambiguationData":[OSD([sQuery(id+"F49.wireOp",EDGE,"E37.left")])]})]});
            var sketch = newSketch(context, id + "F55", { "sketchPlane" : qUnion([Q0])});
            skCircle(sketch, "E40", {"center": v(-200, 2) * mm, "radius": 1 * mm});
            skPoint(sketch, "E40.centerSnap0", {"position": v(-200, 12) * mm});
            skSolve(sketch);
        }
        {
            var Q0;
            Q0=makeQuery(id+"F55.imprint","IMPRINT",FACE,{"disambiguationData":[TD([[makeQuery(id+"F55.imprint","IMPRINT",EDGE,{"derivedFrom":sQuery(id+"F55.wireOp",EDGE,"E40")}),1.0]])]});
            var Q1;
            Q1=sQuery(id+"F55.wireOp",EDGE,"E40");
            extrude(context, id + "F56", {"entities" : qUnion([Q0]), "operationType" : NewBodyOperationType.ADD, "surfaceEntities" : qUnion([Q1]), "depth" : 1.5 * mm});
        }
        {
            var Q0;
            Q0=makeQuery(id+"F50.boolean.opBoolean","MERGE",FACE,{"derivedFrom":[makeQuery(id+"F48.opExtrude","CAP_FACE",FACE,{"disambiguationData":[OSD([sQuery(id+"F47.wireOp",EDGE,"E36.bottom"),sQuery(id+"F47.wireOp",EDGE,"E36.top"),sQuery(id+"F47.wireOp",EDGE,"E36.left"),sQuery(id+"F47.wireOp",EDGE,"E36.right")])],"isStart":true}),makeQuery(id+"F50.opExtrude","SWEPT_FACE",FACE,{"disambiguationData":[OSD([sQuery(id+"F49.wireOp",EDGE,"E37.bottom")])]})]});
            var sketch = newSketch(context, id + "F57", { "sketchPlane" : qUnion([Q0])});
            skCircle(sketch, "E41", {"center": v(200, 0) * mm, "radius": 2.25 * mm});
            skPoint(sketch, "E41.centerSnap0", {"position": v(197, 0) * mm});
            skPoint(sketch, "E41.centerSnap1", {"position": v(200, 6.7) * mm});
            skSolve(sketch);
        }
        {
            var Q0;
            Q0 = qSketchRegion(id + "F57", true);
            extrude(context, id + "F58", {"entities" : qUnion([Q0]), "operationType" : NewBodyOperationType.ADD, "depth" : 2 * mm});
        }
        {
            var Q0;
            Q0=makeQuery(id+"F58.opExtrude","CAP_FACE",FACE,{"disambiguationData":[OSD([sQuery(id+"F57.wireOp",EDGE,"E41")])],"isStart":false});
            var sketch = newSketch(context, id + "F59", { "sketchPlane" : qUnion([Q0])});
            skCircle(sketch, "E42", {"center": v(200, 0) * mm, "radius": 1.35 * mm});
            skSolve(sketch);
        }
        {
            var Q0;
            Q0 = qSketchRegion(id + "F59", true);
            extrude(context, id + "F60", {"entities" : qUnion([Q0]), "operationType" : NewBodyOperationType.ADD, "depth" : 5 * mm});
        }
        {
            var Q0;
            Q0=qCreatedBy(makeId("Top.planeOp"),FACE);
            var sketch = newSketch(context, id + "F61", { "sketchPlane" : qUnion([Q0])});
            skLineSegment(sketch, "E43.bottom", {"start": v(253, 6.7) * mm, "end": v(247, 6.7) * mm});
            skLineSegment(sketch, "E43.top", {"start": v(253, -6.7) * mm, "end": v(247, -6.7) * mm});
            skLineSegment(sketch, "E43.left", {"start": v(253, 6.7) * mm, "end": v(253, -6.7) * mm});
            skLineSegment(sketch, "E43.right", {"start": v(247, 6.7) * mm, "end": v(247, -6.7) * mm});
            skPoint(sketch, "E43.middle", {"position": v(250, 0) * mm});
            skSolve(sketch);
        }
        {
            var Q0;
            Q0 = qSketchRegion(id + "F61", true);
            extrude(context, id + "F62", {"entities" : qUnion([Q0]), "depth" : 16 * mm});
        }
        {
            var Q0;
            Q0=makeQuery(id+"F62.opExtrude","SWEPT_FACE",FACE,{"disambiguationData":[OSD([sQuery(id+"F61.wireOp",EDGE,"E43.left")])]});
            var sketch = newSketch(context, id + "F63", { "sketchPlane" : qUnion([Q0])});
            skLineSegment(sketch, "E44", {"start": v(0, 0) * mm, "end": v(0, 16) * mm, "construction": true});
            skCircle(sketch, "E45", {"center": v(-4, 2) * mm, "radius": 1.25 * mm});
            skCircle(sketch, "E46", {"center": v(4, 2) * mm, "radius": 1.25 * mm});
            skLineSegment(sketch, "E47", {"start": v(-6.7, 2) * mm, "end": v(6.7, 2) * mm, "construction": true});
            skSolve(sketch);
        }
        {
            var Q0;
            Q0 = qSketchRegion(id + "F63", true);
            extrude(context, id + "F64", {"entities" : qUnion([Q0]), "operationType" : NewBodyOperationType.REMOVE, "endBound" : BoundingType.UP_TO_NEXT, "oppositeDirection" : true, "depth" : 25 * mm});
        }
        {
            var Q0;
            Q0=makeQuery(id+"F62.opExtrude","CAP_FACE",FACE,{"disambiguationData":[OSD([sQuery(id+"F61.wireOp",EDGE,"E43.bottom"),sQuery(id+"F61.wireOp",EDGE,"E43.top"),sQuery(id+"F61.wireOp",EDGE,"E43.left"),sQuery(id+"F61.wireOp",EDGE,"E43.right")])],"isStart":false});
            var sketch = newSketch(context, id + "F65", { "sketchPlane" : qUnion([Q0])});
            skLineSegment(sketch, "E48.bottom", {"start": v(253, 2.5) * mm, "end": v(247, 2.5) * mm});
            skLineSegment(sketch, "E48.top", {"start": v(253, -2.5) * mm, "end": v(247, -2.5) * mm});
            skLineSegment(sketch, "E48.left", {"start": v(253, 2.5) * mm, "end": v(253, -2.5) * mm});
            skLineSegment(sketch, "E48.right", {"start": v(247, 2.5) * mm, "end": v(247, -2.5) * mm});
            skPoint(sketch, "E48.middle", {"position": v(250, 0) * mm});
            skPoint(sketch, "E48.middle.positionSnap0", {"position": v(253, 0) * mm});
            skPoint(sketch, "E48.middle.positionSnap1", {"position": v(250, 6.7) * mm});
            skPoint(sketch, "E48.centerSnap0", {"position": v(253, 0) * mm});
            skPoint(sketch, "E48.centerSnap1", {"position": v(250, 6.7) * mm});
            skSolve(sketch);
        }
        {
            var Q0;
            Q0 = qSketchRegion(id + "F65", true);
            extrude(context, id + "F66", {"entities" : qUnion([Q0]), "operationType" : NewBodyOperationType.REMOVE, "oppositeDirection" : true, "depth" : 5.5 * mm});
        }
        {
            var Q0;
            Q0=makeQuery(id+"F62.opExtrude","CAP_FACE",FACE,{"disambiguationData":[OSD([sQuery(id+"F61.wireOp",EDGE,"E43.bottom"),sQuery(id+"F61.wireOp",EDGE,"E43.top"),sQuery(id+"F61.wireOp",EDGE,"E43.left"),sQuery(id+"F61.wireOp",EDGE,"E43.right")])],"isStart":true});
            var sketch = newSketch(context, id + "F67", { "sketchPlane" : qUnion([Q0])});
            skCircle(sketch, "E49", {"center": v(250, 0) * mm, "radius": 1.35 * mm});
            skPoint(sketch, "E49.centerSnap0", {"position": v(250, -6.7) * mm});
            skPoint(sketch, "E49.centerSnap1", {"position": v(253, 0) * mm});
            skSolve(sketch);
        }
        {
            var Q0;
            Q0 = qSketchRegion(id + "F67", true);
            extrude(context, id + "F68", {"entities" : qUnion([Q0]), "operationType" : NewBodyOperationType.ADD, "depth" : 5 * mm});
        }
        {
            var Q0;
            Q0=qCreatedBy(makeId("Top.planeOp"),FACE);
            var sketch = newSketch(context, id + "F69", { "sketchPlane" : qUnion([Q0])});
            skCircle(sketch, "E50", {"center": v(0, -150) * mm, "radius": 2 * mm});
            skSolve(sketch);
        }
        {
            var Q0;
            Q0 = qSketchRegion(id + "F69", true);
            extrude(context, id + "F70", {"entities" : qUnion([Q0]), "depth" : 30 * mm});
        }
        {
            var Q0;
            Q0=makeQuery(id+"F70.opExtrude","CAP_FACE",FACE,{"disambiguationData":[OSD([sQuery(id+"F69.wireOp",EDGE,"E50")])],"isStart":true});
            var sketch = newSketch(context, id + "F71", { "sketchPlane" : qUnion([Q0])});
            skCircle(sketch, "E51", {"center": v(0, 150) * mm, "radius": 1.5 * mm});
            skSolve(sketch);
        }
        {
            var Q0;
            Q0 = qSketchRegion(id + "F71", true);
            extrude(context, id + "F72", {"entities" : qUnion([Q0]), "operationType" : NewBodyOperationType.ADD, "depth" : 10 * mm});
        }
        {
            var Q0;
            Q0=qCreatedBy(makeId("Top.planeOp"),FACE);
            var sketch = newSketch(context, id + "F73", { "sketchPlane" : qUnion([Q0])});
            skLineSegment(sketch, "E52.bottom", {"start": v(50, -150) * mm, "end": v(58, -150) * mm});
            skLineSegment(sketch, "E52.top", {"start": v(50, -122.5) * mm, "end": v(58, -122.5) * mm});
            skLineSegment(sketch, "E52.left", {"start": v(50, -150) * mm, "end": v(50, -122.5) * mm});
            skLineSegment(sketch, "E52.right", {"start": v(58, -150) * mm, "end": v(58, -122.5) * mm});
            skSolve(sketch);
        }
        {
            var Q0;
            Q0 = qSketchRegion(id + "F73", true);
            extrude(context, id + "F74", {"entities" : qUnion([Q0]), "depth" : 6 * mm});
        }
        {
            var Q0;
            Q0=makeQuery(id+"F74.opExtrude","CAP_FACE",FACE,{"disambiguationData":[OSD([sQuery(id+"F73.wireOp",EDGE,"E52.bottom"),sQuery(id+"F73.wireOp",EDGE,"E52.top"),sQuery(id+"F73.wireOp",EDGE,"E52.left"),sQuery(id+"F73.wireOp",EDGE,"E52.right")])],"isStart":false});
            var sketch = newSketch(context, id + "F75", { "sketchPlane" : qUnion([Q0])});
            skLineSegment(sketch, "E53.bottom", {"start": v(50, -122.5) * mm, "end": v(58, -122.5) * mm});
            skLineSegment(sketch, "E53.top", {"start": v(50, -128.4) * mm, "end": v(58, -128.4) * mm});
            skLineSegment(sketch, "E53.left", {"start": v(50, -122.5) * mm, "end": v(50, -128.4) * mm});
            skLineSegment(sketch, "E53.right", {"start": v(58, -122.5) * mm, "end": v(58, -128.4) * mm});
            skSolve(sketch);
        }
        {
            var Q0;
            Q0 = qSketchRegion(id + "F75", true);
            extrude(context, id + "F76", {"entities" : qUnion([Q0]), "operationType" : NewBodyOperationType.ADD, "depth" : 3.5 * mm});
        }
        {
            var Q0;
            Q0=makeQuery(id+"F74.opExtrude","CAP_FACE",FACE,{"disambiguationData":[OSD([sQuery(id+"F73.wireOp",EDGE,"E52.bottom"),sQuery(id+"F73.wireOp",EDGE,"E52.top"),sQuery(id+"F73.wireOp",EDGE,"E52.left"),sQuery(id+"F73.wireOp",EDGE,"E52.right")])],"isStart":false});
            var sketch = newSketch(context, id + "F77", { "sketchPlane" : qUnion([Q0])});
            skPoint(sketch, "E54", {"position": v(54, -142.9) * mm});
            skPoint(sketch, "E54.positionSnap0", {"position": v(54, -150) * mm});
            skSolve(sketch);
        }
        {
            var Q0;
            Q0=sQuery(id+"F77.wireOp",VERTEX,"E54");
            var Q1;
            Q1=makeQuery(id+"F74.opExtrude","SWEPT_BODY",BODY,{"disambiguationData":[OSD([sQuery(id+"F73.wireOp",EDGE,"E52.bottom"),sQuery(id+"F73.wireOp",EDGE,"E52.top"),sQuery(id+"F73.wireOp",EDGE,"E52.left"),sQuery(id+"F73.wireOp",EDGE,"E52.right")])]});
            hole(context, id + "F78", {"style" : HoleStyle.C_BORE, "endStyle" : HoleEndStyle.THROUGH, "holeDiameter" : 2.8 * mm, "cBoreDiameter" : 6.2 * mm, "cBoreDepth" : 1.2 * mm, "startFromSketch" : true, "locations" : qUnion([Q0]), "scope" : qUnion([Q1]), "isTappedThrough" : true});
        }
        {
            var Q0;
            Q0=makeQuery(id+"F74.opExtrude","SWEPT_FACE",FACE,{"disambiguationData":[OSD([sQuery(id+"F73.wireOp",EDGE,"E52.bottom")])]});
            var sketch = newSketch(context, id + "F79", { "sketchPlane" : qUnion([Q0])});
            skCircle(sketch, "E55", {"center": v(54, 3) * mm, "radius": 1.25 * mm});
            skPoint(sketch, "E55.centerSnap0", {"position": v(58, 3) * mm});
            skPoint(sketch, "E55.centerSnap1", {"position": v(54, 0) * mm});
            skSolve(sketch);
        }
        {
            var Q0;
            Q0 = qSketchRegion(id + "F79", true);
            extrude(context, id + "F80", {"entities" : qUnion([Q0]), "operationType" : NewBodyOperationType.ADD, "depth" : 10 * mm});
        }
        {
            var Q0;
            Q0=makeQuery(id+"F76.boolean.opBoolean","MERGE",FACE,{"derivedFrom":[makeQuery(id+"F74.opExtrude","SWEPT_FACE",FACE,{"disambiguationData":[OSD([sQuery(id+"F73.wireOp",EDGE,"E52.top")])]}),makeQuery(id+"F76.opExtrude","SWEPT_FACE",FACE,{"disambiguationData":[OSD([sQuery(id+"F75.wireOp",EDGE,"E53.bottom")])]})]});
            var sketch = newSketch(context, id + "F81", { "sketchPlane" : qUnion([Q0])});
            skLineSegment(sketch, "E56", {"start": v(-54, 9.5) * mm, "end": v(-54, 0) * mm, "construction": true});
            skLineSegment(sketch, "E57", {"start": v(-50, 4.9) * mm, "end": v(-58, 4.9) * mm, "construction": true});
            skLineSegment(sketch, "E58.bottom", {"start": v(-53.5, 9.5) * mm, "end": v(-54.5, 9.5) * mm});
            skLineSegment(sketch, "E58.top", {"start": v(-53.5, 0) * mm, "end": v(-54.5, 0) * mm});
            skLineSegment(sketch, "E58.left", {"start": v(-53.5, 9.5) * mm, "end": v(-53.5, 5.4) * mm});
            skLineSegment(sketch, "E58.right", {"start": v(-54.5, 9.5) * mm, "end": v(-54.5, 5.4) * mm});
            skLineSegment(sketch, "E59.bottom", {"start": v(-50, 4.4) * mm, "end": v(-53.5, 4.4) * mm});
            skLineSegment(sketch, "E59.top", {"start": v(-50, 5.4) * mm, "end": v(-53.5, 5.4) * mm});
            skLineSegment(sketch, "E59.left", {"start": v(-50, 4.4) * mm, "end": v(-50, 5.4) * mm});
            skLineSegment(sketch, "E59.right", {"start": v(-58, 4.4) * mm, "end": v(-58, 5.4) * mm});
            skLineSegment(sketch, "E60.trimOffspring", {"start": v(-53.5, 4.4) * mm, "end": v(-53.5, 0) * mm});
            skLineSegment(sketch, "E61.trimOffspring", {"start": v(-54.5, 5.4) * mm, "end": v(-58, 5.4) * mm});
            skLineSegment(sketch, "E62.trimOffspring", {"start": v(-54.5, 4.4) * mm, "end": v(-58, 4.4) * mm});
            skLineSegment(sketch, "E63.trimOffspring", {"start": v(-54.5, 4.4) * mm, "end": v(-54.5, 0) * mm});
            skSolve(sketch);
        }
        {
            var Q0;
            Q0 = qSketchRegion(id + "F81", true);
            extrude(context, id + "F82", {"entities" : qUnion([Q0]), "operationType" : NewBodyOperationType.REMOVE, "oppositeDirection" : true, "depth" : 0.2 * mm});
        }
        {
            var Q0;
            Q0=makeQuery(id+"F74.opExtrude","CAP_FACE",FACE,{"disambiguationData":[OSD([sQuery(id+"F73.wireOp",EDGE,"E52.bottom"),sQuery(id+"F73.wireOp",EDGE,"E52.top"),sQuery(id+"F73.wireOp",EDGE,"E52.left"),sQuery(id+"F73.wireOp",EDGE,"E52.right")])],"isStart":false});
            var sketch = newSketch(context, id + "F83", { "sketchPlane" : qUnion([Q0])});
            skLineSegment(sketch, "E64", {"start": v(50, -150) * mm, "end": v(50, -148) * mm});
            skLineSegment(sketch, "E65", {"start": v(50, -148) * mm, "end": v(51, -150) * mm});
            skLineSegment(sketch, "E66", {"start": v(51, -150) * mm, "end": v(50, -150) * mm});
            skLineSegment(sketch, "E67", {"start": v(58, -148) * mm, "end": v(57, -150) * mm});
            skLineSegment(sketch, "E68", {"start": v(57, -150) * mm, "end": v(58, -150) * mm});
            skLineSegment(sketch, "E69", {"start": v(58, -150) * mm, "end": v(58, -148) * mm});
            skSolve(sketch);
        }
        {
            var Q0;
            Q0 = qSketchRegion(id + "F83", true);
            extrude(context, id + "F84", {"entities" : qUnion([Q0]), "operationType" : NewBodyOperationType.REMOVE, "endBound" : BoundingType.UP_TO_NEXT, "oppositeDirection" : true, "depth" : 25 * mm});
        }
        {
            var Q0;
            Q0=qCreatedBy(makeId("Top.planeOp"),FACE);
            var sketch = newSketch(context, id + "F85", { "sketchPlane" : qUnion([Q0])});
            skLineSegment(sketch, "E70.bottom", {"start": v(100, -150) * mm, "end": v(108, -150) * mm});
            skLineSegment(sketch, "E70.top", {"start": v(100, -122.5) * mm, "end": v(108, -122.5) * mm});
            skLineSegment(sketch, "E70.left", {"start": v(100, -150) * mm, "end": v(100, -122.5) * mm});
            skLineSegment(sketch, "E70.right", {"start": v(108, -150) * mm, "end": v(108, -122.5) * mm});
            skSolve(sketch);
        }
        {
            var Q0;
            Q0 = qSketchRegion(id + "F85", true);
            extrude(context, id + "F86", {"entities" : qUnion([Q0]), "depth" : 6 * mm});
        }
        {
            var Q0;
            Q0=makeQuery(id+"F86.opExtrude","CAP_FACE",FACE,{"disambiguationData":[OSD([sQuery(id+"F85.wireOp",EDGE,"E70.bottom"),sQuery(id+"F85.wireOp",EDGE,"E70.top"),sQuery(id+"F85.wireOp",EDGE,"E70.left"),sQuery(id+"F85.wireOp",EDGE,"E70.right")])],"isStart":false});
            var sketch = newSketch(context, id + "F87", { "sketchPlane" : qUnion([Q0])});
            skLineSegment(sketch, "E71.bottom", {"start": v(100, -122.5) * mm, "end": v(108, -122.5) * mm});
            skLineSegment(sketch, "E71.top", {"start": v(100, -128.4) * mm, "end": v(108, -128.4) * mm});
            skLineSegment(sketch, "E71.left", {"start": v(100, -122.5) * mm, "end": v(100, -128.4) * mm});
            skLineSegment(sketch, "E71.right", {"start": v(108, -122.5) * mm, "end": v(108, -128.4) * mm});
            skSolve(sketch);
        }
        {
            var Q0;
            Q0 = qSketchRegion(id + "F87", true);
            extrude(context, id + "F88", {"entities" : qUnion([Q0]), "operationType" : NewBodyOperationType.ADD, "depth" : 3.5 * mm});
        }
        {
            var Q0;
            Q0=makeQuery(id+"F86.opExtrude","CAP_FACE",FACE,{"disambiguationData":[OSD([sQuery(id+"F85.wireOp",EDGE,"E70.bottom"),sQuery(id+"F85.wireOp",EDGE,"E70.top"),sQuery(id+"F85.wireOp",EDGE,"E70.left"),sQuery(id+"F85.wireOp",EDGE,"E70.right")])],"isStart":false});
            var sketch = newSketch(context, id + "F89", { "sketchPlane" : qUnion([Q0])});
            skPoint(sketch, "E72", {"position": v(104, -142.9) * mm});
            skPoint(sketch, "E72.positionSnap0", {"position": v(104, -150) * mm});
            skSolve(sketch);
        }
        {
            var Q0;
            Q0=sQuery(id+"F89.wireOp",VERTEX,"E72");
            var Q1;
            Q1=makeQuery(id+"F86.opExtrude","SWEPT_BODY",BODY,{"disambiguationData":[OSD([sQuery(id+"F85.wireOp",EDGE,"E70.bottom"),sQuery(id+"F85.wireOp",EDGE,"E70.top"),sQuery(id+"F85.wireOp",EDGE,"E70.left"),sQuery(id+"F85.wireOp",EDGE,"E70.right")])]});
            hole(context, id + "F90", {"style" : HoleStyle.C_BORE, "endStyle" : HoleEndStyle.THROUGH, "holeDiameter" : 2.8 * mm, "cBoreDiameter" : 6.2 * mm, "cBoreDepth" : 1.2 * mm, "startFromSketch" : true, "locations" : qUnion([Q0]), "scope" : qUnion([Q1]), "isTappedThrough" : true});
        }
        {
            var Q0;
            Q0=makeQuery(id+"F86.opExtrude","SWEPT_FACE",FACE,{"disambiguationData":[OSD([sQuery(id+"F85.wireOp",EDGE,"E70.bottom")])]});
            var sketch = newSketch(context, id + "F91", { "sketchPlane" : qUnion([Q0])});
            skCircle(sketch, "E73", {"center": v(104, 3) * mm, "radius": 1.25 * mm});
            skPoint(sketch, "E73.centerSnap0", {"position": v(108, 3) * mm});
            skPoint(sketch, "E73.centerSnap1", {"position": v(104, 6) * mm});
            skSolve(sketch);
        }
        {
            var Q0;
            Q0 = qSketchRegion(id + "F91", true);
            extrude(context, id + "F92", {"entities" : qUnion([Q0]), "operationType" : NewBodyOperationType.ADD, "depth" : 10 * mm});
        }
        {
            var Q0;
            Q0=makeQuery(id+"F88.boolean.opBoolean","MERGE",FACE,{"derivedFrom":[makeQuery(id+"F86.opExtrude","SWEPT_FACE",FACE,{"disambiguationData":[OSD([sQuery(id+"F85.wireOp",EDGE,"E70.top")])]}),makeQuery(id+"F88.opExtrude","SWEPT_FACE",FACE,{"disambiguationData":[OSD([sQuery(id+"F87.wireOp",EDGE,"E71.bottom")])]})]});
            var sketch = newSketch(context, id + "F93", { "sketchPlane" : qUnion([Q0])});
            skLineSegment(sketch, "E74", {"start": v(-104, 0) * mm, "end": v(-104, 9.5) * mm, "construction": true});
            skLineSegment(sketch, "E75", {"start": v(-108, 4.9) * mm, "end": v(-100, 4.9) * mm, "construction": true});
            skLineSegment(sketch, "E76.bottom", {"start": v(-103.5, 0) * mm, "end": v(-104.5, 0) * mm});
            skLineSegment(sketch, "E76.top", {"start": v(-103.5, 9.5) * mm, "end": v(-104.5, 9.5) * mm});
            skLineSegment(sketch, "E76.left", {"start": v(-103.5, 0) * mm, "end": v(-103.5, 4.4) * mm});
            skLineSegment(sketch, "E76.right", {"start": v(-104.5, 0) * mm, "end": v(-104.5, 4.4) * mm});
            skLineSegment(sketch, "E77.bottom", {"start": v(-100, 4.4) * mm, "end": v(-103.5, 4.4) * mm});
            skLineSegment(sketch, "E77.top", {"start": v(-100, 5.4) * mm, "end": v(-103.5, 5.4) * mm});
            skLineSegment(sketch, "E77.left", {"start": v(-100, 4.4) * mm, "end": v(-100, 5.4) * mm});
            skLineSegment(sketch, "E77.right", {"start": v(-108, 4.4) * mm, "end": v(-108, 5.4) * mm});
            skLineSegment(sketch, "E78.trimOffspring", {"start": v(-104.5, 4.4) * mm, "end": v(-108, 4.4) * mm});
            skLineSegment(sketch, "E79.trimOffspring", {"start": v(-103.5, 5.4) * mm, "end": v(-103.5, 9.5) * mm});
            skLineSegment(sketch, "E80.trimOffspring", {"start": v(-104.5, 5.4) * mm, "end": v(-108, 5.4) * mm});
            skLineSegment(sketch, "E81.trimOffspring", {"start": v(-104.5, 5.4) * mm, "end": v(-104.5, 9.5) * mm});
            skSolve(sketch);
        }
        {
            var Q0;
            Q0 = qSketchRegion(id + "F93", true);
            extrude(context, id + "F94", {"entities" : qUnion([Q0]), "operationType" : NewBodyOperationType.REMOVE, "oppositeDirection" : true, "depth" : 0.2 * mm});
        }
        {
            var Q0;
            Q0=makeQuery(id+"F86.opExtrude","CAP_FACE",FACE,{"disambiguationData":[OSD([sQuery(id+"F85.wireOp",EDGE,"E70.bottom"),sQuery(id+"F85.wireOp",EDGE,"E70.top"),sQuery(id+"F85.wireOp",EDGE,"E70.left"),sQuery(id+"F85.wireOp",EDGE,"E70.right")])],"isStart":false});
            var sketch = newSketch(context, id + "F95", { "sketchPlane" : qUnion([Q0])});
            skLineSegment(sketch, "E82", {"start": v(100, -148) * mm, "end": v(101, -150) * mm});
            skLineSegment(sketch, "E83", {"start": v(101, -150) * mm, "end": v(100, -150) * mm});
            skLineSegment(sketch, "E84", {"start": v(100, -150) * mm, "end": v(100, -148) * mm});
            skLineSegment(sketch, "E85", {"start": v(108, -148) * mm, "end": v(107, -150) * mm});
            skLineSegment(sketch, "E86", {"start": v(107, -150) * mm, "end": v(108, -150) * mm});
            skLineSegment(sketch, "E87", {"start": v(108, -150) * mm, "end": v(108, -148) * mm});
            skSolve(sketch);
        }
        {
            var Q0;
            Q0 = qSketchRegion(id + "F95", true);
            extrude(context, id + "F96", {"entities" : qUnion([Q0]), "operationType" : NewBodyOperationType.REMOVE, "endBound" : BoundingType.UP_TO_NEXT, "oppositeDirection" : true, "depth" : 25 * mm});
        }
        {
            var Q0;
            Q0=makeQuery(id+"F86.opExtrude","CAP_FACE",FACE,{"disambiguationData":[OSD([sQuery(id+"F85.wireOp",EDGE,"E70.bottom"),sQuery(id+"F85.wireOp",EDGE,"E70.top"),sQuery(id+"F85.wireOp",EDGE,"E70.left"),sQuery(id+"F85.wireOp",EDGE,"E70.right")])],"isStart":true});
            var sketch = newSketch(context, id + "F97", { "sketchPlane" : qUnion([Q0])});
            skCircle(sketch, "E88", {"center": v(104, 128.9) * mm, "radius": 1 * mm});
            skSolve(sketch);
        }
        {
            var Q0;
            Q0 = qSketchRegion(id + "F97", true);
            extrude(context, id + "F98", {"entities" : qUnion([Q0]), "operationType" : NewBodyOperationType.ADD, "depth" : 1.6 * mm});
        }
        {
            var Q0;
            Q0=qCreatedBy(makeId("Top.planeOp"),FACE);
            var sketch = newSketch(context, id + "F99", { "sketchPlane" : qUnion([Q0])});
            skLineSegment(sketch, "E89.bottom", {"start": v(150, -150) * mm, "end": v(158, -150) * mm});
            skLineSegment(sketch, "E89.top", {"start": v(150, -125) * mm, "end": v(158, -125) * mm});
            skLineSegment(sketch, "E89.left", {"start": v(150, -150) * mm, "end": v(150, -125) * mm});
            skLineSegment(sketch, "E89.right", {"start": v(158, -150) * mm, "end": v(158, -125) * mm});
            skSolve(sketch);
        }
        {
            var Q0;
            Q0 = qSketchRegion(id + "F99", true);
            extrude(context, id + "F100", {"entities" : qUnion([Q0]), "depth" : 6 * mm});
        }
        {
            var Q0;
            Q0=makeQuery(id+"F100.opExtrude","CAP_FACE",FACE,{"disambiguationData":[OSD([sQuery(id+"F99.wireOp",EDGE,"E89.bottom"),sQuery(id+"F99.wireOp",EDGE,"E89.top"),sQuery(id+"F99.wireOp",EDGE,"E89.left"),sQuery(id+"F99.wireOp",EDGE,"E89.right")])],"isStart":false});
            var sketch = newSketch(context, id + "F101", { "sketchPlane" : qUnion([Q0])});
            skPoint(sketch, "E90", {"position": v(154, -142.9) * mm});
            skPoint(sketch, "E90.positionSnap0", {"position": v(154, -125) * mm});
            skSolve(sketch);
        }
        {
            var Q0;
            Q0=sQuery(id+"F101.wireOp",VERTEX,"E90");
            var Q1;
            Q1=makeQuery(id+"F100.opExtrude","SWEPT_BODY",BODY,{"disambiguationData":[OSD([sQuery(id+"F99.wireOp",EDGE,"E89.bottom"),sQuery(id+"F99.wireOp",EDGE,"E89.top"),sQuery(id+"F99.wireOp",EDGE,"E89.left"),sQuery(id+"F99.wireOp",EDGE,"E89.right")])]});
            hole(context, id + "F102", {"style" : HoleStyle.C_BORE, "endStyle" : HoleEndStyle.THROUGH, "holeDiameter" : 2.8 * mm, "cBoreDiameter" : 6.2 * mm, "cBoreDepth" : 1.7 * mm, "startFromSketch" : true, "locations" : qUnion([Q0]), "scope" : qUnion([Q1]), "isTappedThrough" : true});
        }
        {
            var Q0;
            Q0=makeQuery(id+"F100.opExtrude","CAP_FACE",FACE,{"disambiguationData":[OSD([sQuery(id+"F99.wireOp",EDGE,"E89.bottom"),sQuery(id+"F99.wireOp",EDGE,"E89.top"),sQuery(id+"F99.wireOp",EDGE,"E89.left"),sQuery(id+"F99.wireOp",EDGE,"E89.right")])],"isStart":false});
            var sketch = newSketch(context, id + "F103", { "sketchPlane" : qUnion([Q0])});
            skLineSegment(sketch, "E91", {"start": v(154, -125) * mm, "end": v(154, -136.68) * mm, "construction": true});
            skLineSegment(sketch, "E92", {"start": v(158, -128.9) * mm, "end": v(150, -128.9) * mm, "construction": true});
            skLineSegment(sketch, "E93.bottom", {"start": v(153.5, -125) * mm, "end": v(154.5, -125) * mm});
            skLineSegment(sketch, "E93.top", {"start": v(153.5, -133) * mm, "end": v(154.5, -133) * mm});
            skLineSegment(sketch, "E93.left", {"start": v(153.5, -125) * mm, "end": v(153.5, -128.4) * mm});
            skLineSegment(sketch, "E93.right", {"start": v(154.5, -125) * mm, "end": v(154.5, -128.4) * mm});
            skLineSegment(sketch, "E94.bottom", {"start": v(158, -128.4) * mm, "end": v(154.5, -128.4) * mm});
            skLineSegment(sketch, "E94.top", {"start": v(158, -129.4) * mm, "end": v(154.5, -129.4) * mm});
            skLineSegment(sketch, "E94.left", {"start": v(158, -128.4) * mm, "end": v(158, -129.4) * mm});
            skLineSegment(sketch, "E94.right", {"start": v(150, -128.4) * mm, "end": v(150, -129.4) * mm});
            skLineSegment(sketch, "E95.trimOffspring", {"start": v(153.5, -129.4) * mm, "end": v(153.5, -133) * mm});
            skLineSegment(sketch, "E96.trimOffspring", {"start": v(153.5, -128.4) * mm, "end": v(150, -128.4) * mm});
            skLineSegment(sketch, "E97.trimOffspring", {"start": v(154.5, -129.4) * mm, "end": v(154.5, -133) * mm});
            skLineSegment(sketch, "E98.trimOffspring", {"start": v(153.5, -129.4) * mm, "end": v(150, -129.4) * mm});
            skSolve(sketch);
        }
        {
            var Q0;
            Q0 = qSketchRegion(id + "F103", true);
            extrude(context, id + "F104", {"entities" : qUnion([Q0]), "operationType" : NewBodyOperationType.REMOVE, "oppositeDirection" : true, "depth" : 0.2 * mm});
        }
        {
            var Q0;
            Q0=makeQuery(id+"F100.opExtrude","SWEPT_FACE",FACE,{"disambiguationData":[OSD([sQuery(id+"F99.wireOp",EDGE,"E89.bottom")])]});
            var sketch = newSketch(context, id + "F105", { "sketchPlane" : qUnion([Q0])});
            skCircle(sketch, "E99", {"center": v(154, 3) * mm, "radius": 1.25 * mm});
            skPoint(sketch, "E99.centerSnap0", {"position": v(158, 3) * mm});
            skPoint(sketch, "E99.centerSnap1", {"position": v(154, 6) * mm});
            skSolve(sketch);
        }
        {
            var Q0;
            Q0 = qSketchRegion(id + "F105", true);
            extrude(context, id + "F106", {"entities" : qUnion([Q0]), "operationType" : NewBodyOperationType.ADD, "depth" : 10 * mm});
        }
        {
            var Q0;
            {var subQ0=sQuery(id+"F99.wireOp",EDGE,"E89.right");var subQ1=sQuery(id+"F99.wireOp",EDGE,"E89.left");var subQ2=sQuery(id+"F99.wireOp",EDGE,"E89.bottom");Q0=makeQuery(id+"F104.boolean.opBoolean","SPLIT",FACE,{"disambiguationData":[TD([makeQuery(id+"F100.opExtrude","SWEPT_FACE",FACE,{"disambiguationData":[OSD([subQ2])]})])],"derivedFrom":makeQuery(id+"F100.opExtrude","CAP_FACE",FACE,{"disambiguationData":[OSD([subQ2,sQuery(id+"F99.wireOp",EDGE,"E89.top"),subQ1,subQ0])],"isStart":false})});}
            var sketch = newSketch(context, id + "F107", { "sketchPlane" : qUnion([Q0])});
            skLineSegment(sketch, "E100", {"start": v(150, -148) * mm, "end": v(151, -150) * mm});
            skLineSegment(sketch, "E101", {"start": v(151, -150) * mm, "end": v(150, -150) * mm});
            skLineSegment(sketch, "E102", {"start": v(150, -150) * mm, "end": v(150, -148) * mm});
            skLineSegment(sketch, "E103", {"start": v(158, -148) * mm, "end": v(158, -150) * mm});
            skLineSegment(sketch, "E104", {"start": v(158, -150) * mm, "end": v(157, -150) * mm});
            skLineSegment(sketch, "E105", {"start": v(157, -150) * mm, "end": v(158, -148) * mm});
            skSolve(sketch);
        }
        {
            var Q0;
            Q0 = qSketchRegion(id + "F107", true);
            extrude(context, id + "F108", {"entities" : qUnion([Q0]), "operationType" : NewBodyOperationType.REMOVE, "endBound" : BoundingType.UP_TO_NEXT, "oppositeDirection" : true, "depth" : 25 * mm});
        }
        {
            var Q0;
            Q0=qCreatedBy(makeId("Top.planeOp"),FACE);
            var sketch = newSketch(context, id + "F109", { "sketchPlane" : qUnion([Q0])});
            skLineSegment(sketch, "E106.bottom", {"start": v(200, -150) * mm, "end": v(208, -150) * mm});
            skLineSegment(sketch, "E106.top", {"start": v(200, -125) * mm, "end": v(208, -125) * mm});
            skLineSegment(sketch, "E106.left", {"start": v(200, -150) * mm, "end": v(200, -125) * mm});
            skLineSegment(sketch, "E106.right", {"start": v(208, -150) * mm, "end": v(208, -125) * mm});
            skSolve(sketch);
        }
        {
            var Q0;
            Q0 = qSketchRegion(id + "F109", true);
            extrude(context, id + "F110", {"entities" : qUnion([Q0]), "depth" : 6 * mm});
        }
        {
            var Q0;
            Q0=makeQuery(id+"F110.opExtrude","CAP_FACE",FACE,{"disambiguationData":[OSD([sQuery(id+"F109.wireOp",EDGE,"E106.bottom"),sQuery(id+"F109.wireOp",EDGE,"E106.top"),sQuery(id+"F109.wireOp",EDGE,"E106.left"),sQuery(id+"F109.wireOp",EDGE,"E106.right")])],"isStart":false});
            var sketch = newSketch(context, id + "F111", { "sketchPlane" : qUnion([Q0])});
            skPoint(sketch, "E107", {"position": v(204, -142.9) * mm});
            skPoint(sketch, "E107.positionSnap0", {"position": v(204, -125) * mm});
            skSolve(sketch);
        }
        {
            var Q0;
            Q0=sQuery(id+"F111.wireOp",VERTEX,"E107");
            var Q1;
            Q1=makeQuery(id+"F110.opExtrude","SWEPT_BODY",BODY,{"disambiguationData":[OSD([sQuery(id+"F109.wireOp",EDGE,"E106.bottom"),sQuery(id+"F109.wireOp",EDGE,"E106.top"),sQuery(id+"F109.wireOp",EDGE,"E106.left"),sQuery(id+"F109.wireOp",EDGE,"E106.right")])]});
            hole(context, id + "F112", {"style" : HoleStyle.C_BORE, "endStyle" : HoleEndStyle.THROUGH, "holeDiameter" : 2.8 * mm, "cBoreDiameter" : 6.2 * mm, "cBoreDepth" : 1.7 * mm, "startFromSketch" : true, "locations" : qUnion([Q0]), "scope" : qUnion([Q1]), "isTappedThrough" : true});
        }
        {
            var Q0;
            Q0=makeQuery(id+"F110.opExtrude","CAP_FACE",FACE,{"disambiguationData":[OSD([sQuery(id+"F109.wireOp",EDGE,"E106.bottom"),sQuery(id+"F109.wireOp",EDGE,"E106.top"),sQuery(id+"F109.wireOp",EDGE,"E106.left"),sQuery(id+"F109.wireOp",EDGE,"E106.right")])],"isStart":false});
            var sketch = newSketch(context, id + "F113", { "sketchPlane" : qUnion([Q0])});
            skLineSegment(sketch, "E108", {"start": v(200, -128.9) * mm, "end": v(208, -128.9) * mm, "construction": true});
            skLineSegment(sketch, "E109", {"start": v(204, -125) * mm, "end": v(204, -135.4) * mm, "construction": true});
            skLineSegment(sketch, "E110.bottom", {"start": v(203.5, -125) * mm, "end": v(204.5, -125) * mm});
            skLineSegment(sketch, "E110.top", {"start": v(203.5, -133) * mm, "end": v(204.5, -133) * mm});
            skLineSegment(sketch, "E110.left", {"start": v(203.5, -125) * mm, "end": v(203.5, -128.4) * mm});
            skLineSegment(sketch, "E110.right", {"start": v(204.5, -125) * mm, "end": v(204.5, -128.4) * mm});
            skLineSegment(sketch, "E111.bottom", {"start": v(208, -128.4) * mm, "end": v(204.5, -128.4) * mm});
            skLineSegment(sketch, "E111.top", {"start": v(208, -129.4) * mm, "end": v(204.5, -129.4) * mm});
            skLineSegment(sketch, "E111.left", {"start": v(208, -128.4) * mm, "end": v(208, -129.4) * mm});
            skLineSegment(sketch, "E111.right", {"start": v(200, -128.4) * mm, "end": v(200, -129.4) * mm});
            skLineSegment(sketch, "E112.trimOffspring", {"start": v(203.5, -128.4) * mm, "end": v(200, -128.4) * mm});
            skLineSegment(sketch, "E113.trimOffspring", {"start": v(203.5, -129.4) * mm, "end": v(203.5, -133) * mm});
            skLineSegment(sketch, "E114.trimOffspring", {"start": v(203.5, -129.4) * mm, "end": v(200, -129.4) * mm});
            skLineSegment(sketch, "E115.trimOffspring", {"start": v(204.5, -129.4) * mm, "end": v(204.5, -133) * mm});
            skSolve(sketch);
        }
        {
            var Q0;
            Q0 = qSketchRegion(id + "F113", true);
            extrude(context, id + "F114", {"entities" : qUnion([Q0]), "operationType" : NewBodyOperationType.REMOVE, "oppositeDirection" : true, "depth" : 0.2 * mm});
        }
        {
            var Q0;
            Q0=makeQuery(id+"F110.opExtrude","SWEPT_FACE",FACE,{"disambiguationData":[OSD([sQuery(id+"F109.wireOp",EDGE,"E106.bottom")])]});
            var sketch = newSketch(context, id + "F115", { "sketchPlane" : qUnion([Q0])});
            skCircle(sketch, "E116", {"center": v(204, 3) * mm, "radius": 1.25 * mm});
            skPoint(sketch, "E116.centerSnap0", {"position": v(208, 3) * mm});
            skPoint(sketch, "E116.centerSnap1", {"position": v(204, 6) * mm});
            skSolve(sketch);
        }
        {
            var Q0;
            Q0 = qSketchRegion(id + "F115", true);
            extrude(context, id + "F116", {"entities" : qUnion([Q0]), "operationType" : NewBodyOperationType.ADD, "depth" : 10 * mm});
        }
        {
            var Q0;
            Q0=makeQuery(id+"F110.opExtrude","CAP_FACE",FACE,{"disambiguationData":[OSD([sQuery(id+"F109.wireOp",EDGE,"E106.bottom"),sQuery(id+"F109.wireOp",EDGE,"E106.top"),sQuery(id+"F109.wireOp",EDGE,"E106.left"),sQuery(id+"F109.wireOp",EDGE,"E106.right")])],"isStart":true});
            var sketch = newSketch(context, id + "F117", { "sketchPlane" : qUnion([Q0])});
            skCircle(sketch, "E117", {"center": v(204, 128.9) * mm, "radius": 1 * mm});
            skPoint(sketch, "E117.centerSnap0", {"position": v(204, 125) * mm});
            skSolve(sketch);
        }
        {
            var Q0;
            Q0 = qSketchRegion(id + "F117", true);
            extrude(context, id + "F118", {"entities" : qUnion([Q0]), "operationType" : NewBodyOperationType.ADD, "depth" : 1.6 * mm});
        }
        {
            var Q0;
            {var subQ0=sQuery(id+"F109.wireOp",EDGE,"E106.right");var subQ1=sQuery(id+"F109.wireOp",EDGE,"E106.left");var subQ2=sQuery(id+"F109.wireOp",EDGE,"E106.bottom");Q0=makeQuery(id+"F114.boolean.opBoolean","SPLIT",FACE,{"disambiguationData":[TD([makeQuery(id+"F110.opExtrude","SWEPT_FACE",FACE,{"disambiguationData":[OSD([subQ2])]})])],"derivedFrom":makeQuery(id+"F110.opExtrude","CAP_FACE",FACE,{"disambiguationData":[OSD([subQ2,sQuery(id+"F109.wireOp",EDGE,"E106.top"),subQ1,subQ0])],"isStart":false})});}
            var sketch = newSketch(context, id + "F119", { "sketchPlane" : qUnion([Q0])});
            skLineSegment(sketch, "E118", {"start": v(200, -148) * mm, "end": v(201, -150) * mm});
            skLineSegment(sketch, "E119", {"start": v(201, -150) * mm, "end": v(200, -150) * mm});
            skLineSegment(sketch, "E120", {"start": v(200, -150) * mm, "end": v(200, -148) * mm});
            skLineSegment(sketch, "E121", {"start": v(208, -148) * mm, "end": v(207, -150) * mm});
            skLineSegment(sketch, "E122", {"start": v(207, -150) * mm, "end": v(208, -150) * mm});
            skLineSegment(sketch, "E123", {"start": v(208, -150) * mm, "end": v(208, -148) * mm});
            skSolve(sketch);
        }
        {
            var Q0;
            Q0 = qSketchRegion(id + "F119", true);
            extrude(context, id + "F120", {"entities" : qUnion([Q0]), "operationType" : NewBodyOperationType.REMOVE, "endBound" : BoundingType.UP_TO_NEXT, "oppositeDirection" : true, "depth" : 25 * mm});
        }
        {
            var Q0;
            Q0=qCreatedBy(makeId("Top.planeOp"),FACE);
            var sketch = newSketch(context, id + "F121", { "sketchPlane" : qUnion([Q0])});
            skLineSegment(sketch, "E124.bottom", {"start": v(250, -150) * mm, "end": v(258, -150) * mm});
            skLineSegment(sketch, "E124.top", {"start": v(250, -125) * mm, "end": v(258, -125) * mm});
            skLineSegment(sketch, "E124.left", {"start": v(250, -150) * mm, "end": v(250, -125) * mm});
            skLineSegment(sketch, "E124.right", {"start": v(258, -150) * mm, "end": v(258, -125) * mm});
            skSolve(sketch);
        }
        {
            var Q0;
            Q0 = qSketchRegion(id + "F121", true);
            extrude(context, id + "F122", {"entities" : qUnion([Q0]), "depth" : 6 * mm});
        }
        {
            var Q0;
            Q0=makeQuery(id+"F122.opExtrude","CAP_FACE",FACE,{"disambiguationData":[OSD([sQuery(id+"F121.wireOp",EDGE,"E124.bottom"),sQuery(id+"F121.wireOp",EDGE,"E124.top"),sQuery(id+"F121.wireOp",EDGE,"E124.left"),sQuery(id+"F121.wireOp",EDGE,"E124.right")])],"isStart":false});
            var sketch = newSketch(context, id + "F123", { "sketchPlane" : qUnion([Q0])});
            skPoint(sketch, "E125", {"position": v(254, -142.9) * mm});
            skPoint(sketch, "E125.positionSnap0", {"position": v(254, -125) * mm});
            skSolve(sketch);
        }
        {
            var Q0;
            Q0=sQuery(id+"F123.wireOp",VERTEX,"E125");
            var Q1;
            Q1=makeQuery(id+"F122.opExtrude","SWEPT_BODY",BODY,{"disambiguationData":[OSD([sQuery(id+"F121.wireOp",EDGE,"E124.bottom"),sQuery(id+"F121.wireOp",EDGE,"E124.top"),sQuery(id+"F121.wireOp",EDGE,"E124.left"),sQuery(id+"F121.wireOp",EDGE,"E124.right")])]});
            hole(context, id + "F124", {"style" : HoleStyle.C_BORE, "endStyle" : HoleEndStyle.THROUGH, "holeDiameter" : 2.8 * mm, "cBoreDiameter" : 6.2 * mm, "cBoreDepth" : 1.2 * mm, "startFromSketch" : true, "locations" : qUnion([Q0]), "scope" : qUnion([Q1]), "isTappedThrough" : true});
        }
        {
            var Q0;
            Q0=makeQuery(id+"F122.opExtrude","CAP_FACE",FACE,{"disambiguationData":[OSD([sQuery(id+"F121.wireOp",EDGE,"E124.bottom"),sQuery(id+"F121.wireOp",EDGE,"E124.top"),sQuery(id+"F121.wireOp",EDGE,"E124.left"),sQuery(id+"F121.wireOp",EDGE,"E124.right")])],"isStart":false});
            var sketch = newSketch(context, id + "F125", { "sketchPlane" : qUnion([Q0])});
            skLineSegment(sketch, "E126.bottom", {"start": v(250, -125) * mm, "end": v(258, -125) * mm});
            skLineSegment(sketch, "E126.top", {"start": v(250, -132.8) * mm, "end": v(258, -132.8) * mm});
            skLineSegment(sketch, "E126.left", {"start": v(250, -125) * mm, "end": v(250, -132.8) * mm});
            skLineSegment(sketch, "E126.right", {"start": v(258, -125) * mm, "end": v(258, -132.8) * mm});
            skSolve(sketch);
        }
        {
            var Q0;
            Q0 = qSketchRegion(id + "F125", true);
            extrude(context, id + "F126", {"entities" : qUnion([Q0]), "operationType" : NewBodyOperationType.ADD, "depth" : 1.5 * mm});
        }
        {
            var Q0;
            Q0=makeQuery(id+"F126.opExtrude","CAP_FACE",FACE,{"disambiguationData":[OSD([sQuery(id+"F125.wireOp",EDGE,"E126.bottom"),sQuery(id+"F125.wireOp",EDGE,"E126.top"),sQuery(id+"F125.wireOp",EDGE,"E126.left"),sQuery(id+"F125.wireOp",EDGE,"E126.right")])],"isStart":false});
            var sketch = newSketch(context, id + "F127", { "sketchPlane" : qUnion([Q0])});
            skLineSegment(sketch, "E127", {"start": v(254, -125) * mm, "end": v(254, -132.8) * mm, "construction": true});
            skLineSegment(sketch, "E128", {"start": v(258, -128.9) * mm, "end": v(250, -128.9) * mm, "construction": true});
            skLineSegment(sketch, "E129.bottom", {"start": v(253.5, -125) * mm, "end": v(254.5, -125) * mm});
            skLineSegment(sketch, "E129.top", {"start": v(253.5, -132.8) * mm, "end": v(254.5, -132.8) * mm});
            skLineSegment(sketch, "E129.left", {"start": v(253.5, -125) * mm, "end": v(253.5, -128.4) * mm});
            skLineSegment(sketch, "E129.right", {"start": v(254.5, -125) * mm, "end": v(254.5, -128.4) * mm});
            skLineSegment(sketch, "E130.bottom", {"start": v(258, -128.4) * mm, "end": v(254.5, -128.4) * mm});
            skLineSegment(sketch, "E130.top", {"start": v(258, -129.4) * mm, "end": v(254.5, -129.4) * mm});
            skLineSegment(sketch, "E130.left", {"start": v(258, -128.4) * mm, "end": v(258, -129.4) * mm});
            skLineSegment(sketch, "E130.right", {"start": v(250, -128.4) * mm, "end": v(250, -129.4) * mm});
            skLineSegment(sketch, "E131.trimOffspring", {"start": v(253.5, -128.4) * mm, "end": v(250, -128.4) * mm});
            skLineSegment(sketch, "E132.trimOffspring", {"start": v(253.5, -129.4) * mm, "end": v(253.5, -132.8) * mm});
            skLineSegment(sketch, "E133.trimOffspring", {"start": v(253.5, -129.4) * mm, "end": v(250, -129.4) * mm});
            skLineSegment(sketch, "E134.trimOffspring", {"start": v(254.5, -129.4) * mm, "end": v(254.5, -132.8) * mm});
            skSolve(sketch);
        }
        {
            var Q0;
            Q0 = qSketchRegion(id + "F127", true);
            extrude(context, id + "F128", {"entities" : qUnion([Q0]), "operationType" : NewBodyOperationType.REMOVE, "oppositeDirection" : true, "depth" : 0.2 * mm});
        }
        {
            var Q0;
            Q0=makeQuery(id+"F122.opExtrude","SWEPT_FACE",FACE,{"disambiguationData":[OSD([sQuery(id+"F121.wireOp",EDGE,"E124.bottom")])]});
            var sketch = newSketch(context, id + "F129", { "sketchPlane" : qUnion([Q0])});
            skCircle(sketch, "E135", {"center": v(254, 3) * mm, "radius": 1.25 * mm});
            skPoint(sketch, "E135.centerSnap0", {"position": v(258, 3) * mm});
            skPoint(sketch, "E135.centerSnap1", {"position": v(254, 6) * mm});
            skSolve(sketch);
        }
        {
            var Q0;
            Q0 = qSketchRegion(id + "F129", true);
            extrude(context, id + "F130", {"entities" : qUnion([Q0]), "operationType" : NewBodyOperationType.ADD, "depth" : 10 * mm});
        }
        {
            var Q0;
            Q0=qCreatedBy(makeId("Top.planeOp"),FACE);
            var sketch = newSketch(context, id + "F131", { "sketchPlane" : qUnion([Q0])});
            skLineSegment(sketch, "E136.bottom", {"start": v(300, -150) * mm, "end": v(308, -150) * mm});
            skLineSegment(sketch, "E136.top", {"start": v(300, -125) * mm, "end": v(308, -125) * mm});
            skLineSegment(sketch, "E136.left", {"start": v(300, -150) * mm, "end": v(300, -125) * mm});
            skLineSegment(sketch, "E136.right", {"start": v(308, -150) * mm, "end": v(308, -125) * mm});
            skSolve(sketch);
        }
        {
            var Q0;
            Q0 = qSketchRegion(id + "F131", true);
            extrude(context, id + "F132", {"entities" : qUnion([Q0]), "depth" : 6 * mm});
        }
        {
            var Q0;
            Q0=makeQuery(id+"F132.opExtrude","CAP_FACE",FACE,{"disambiguationData":[OSD([sQuery(id+"F131.wireOp",EDGE,"E136.bottom"),sQuery(id+"F131.wireOp",EDGE,"E136.top"),sQuery(id+"F131.wireOp",EDGE,"E136.left"),sQuery(id+"F131.wireOp",EDGE,"E136.right")])],"isStart":false});
            var sketch = newSketch(context, id + "F133", { "sketchPlane" : qUnion([Q0])});
            skPoint(sketch, "E137", {"position": v(304, -142.9) * mm});
            skPoint(sketch, "E137.positionSnap0", {"position": v(304, -125) * mm});
            skSolve(sketch);
        }
        {
            var Q0;
            Q0=sQuery(id+"F133.wireOp",VERTEX,"E137");
            var Q1;
            Q1=makeQuery(id+"F132.opExtrude","SWEPT_BODY",BODY,{"disambiguationData":[OSD([sQuery(id+"F131.wireOp",EDGE,"E136.bottom"),sQuery(id+"F131.wireOp",EDGE,"E136.top"),sQuery(id+"F131.wireOp",EDGE,"E136.left"),sQuery(id+"F131.wireOp",EDGE,"E136.right")])]});
            hole(context, id + "F134", {"style" : HoleStyle.C_BORE, "endStyle" : HoleEndStyle.THROUGH, "holeDiameter" : 2.8 * mm, "cBoreDiameter" : 6.2 * mm, "cBoreDepth" : 1.2 * mm, "startFromSketch" : true, "locations" : qUnion([Q0]), "scope" : qUnion([Q1]), "isTappedThrough" : true});
        }
        {
            var Q0;
            Q0=makeQuery(id+"F132.opExtrude","CAP_FACE",FACE,{"disambiguationData":[OSD([sQuery(id+"F131.wireOp",EDGE,"E136.bottom"),sQuery(id+"F131.wireOp",EDGE,"E136.top"),sQuery(id+"F131.wireOp",EDGE,"E136.left"),sQuery(id+"F131.wireOp",EDGE,"E136.right")])],"isStart":false});
            var sketch = newSketch(context, id + "F135", { "sketchPlane" : qUnion([Q0])});
            skLineSegment(sketch, "E138.bottom", {"start": v(300, -125) * mm, "end": v(308, -125) * mm});
            skLineSegment(sketch, "E138.top", {"start": v(300, -132.8) * mm, "end": v(308, -132.8) * mm});
            skLineSegment(sketch, "E138.left", {"start": v(300, -125) * mm, "end": v(300, -132.8) * mm});
            skLineSegment(sketch, "E138.right", {"start": v(308, -125) * mm, "end": v(308, -132.8) * mm});
            skSolve(sketch);
        }
        {
            var Q0;
            Q0 = qSketchRegion(id + "F135", true);
            extrude(context, id + "F136", {"entities" : qUnion([Q0]), "operationType" : NewBodyOperationType.ADD, "depth" : 1.5 * mm});
        }
        {
            var Q0;
            Q0=makeQuery(id+"F136.opExtrude","CAP_FACE",FACE,{"disambiguationData":[OSD([sQuery(id+"F135.wireOp",EDGE,"E138.bottom"),sQuery(id+"F135.wireOp",EDGE,"E138.top"),sQuery(id+"F135.wireOp",EDGE,"E138.left"),sQuery(id+"F135.wireOp",EDGE,"E138.right")])],"isStart":false});
            var sketch = newSketch(context, id + "F137", { "sketchPlane" : qUnion([Q0])});
            skLineSegment(sketch, "E139", {"start": v(304, -125) * mm, "end": v(304, -132.8) * mm, "construction": true});
            skLineSegment(sketch, "E140", {"start": v(308, -128.9) * mm, "end": v(300, -128.9) * mm, "construction": true});
            skLineSegment(sketch, "E141.bottom", {"start": v(303.5, -125) * mm, "end": v(304.5, -125) * mm});
            skLineSegment(sketch, "E141.top", {"start": v(303.5, -132.8) * mm, "end": v(304.5, -132.8) * mm});
            skLineSegment(sketch, "E141.left", {"start": v(303.5, -125) * mm, "end": v(303.5, -132.8) * mm});
            skLineSegment(sketch, "E141.right", {"start": v(304.5, -125) * mm, "end": v(304.5, -132.8) * mm});
            skLineSegment(sketch, "E142.bottom", {"start": v(308, -128.4) * mm, "end": v(300, -128.4) * mm});
            skLineSegment(sketch, "E142.top", {"start": v(308, -129.4) * mm, "end": v(300, -129.4) * mm});
            skLineSegment(sketch, "E142.left", {"start": v(308, -128.4) * mm, "end": v(308, -129.4) * mm});
            skLineSegment(sketch, "E142.right", {"start": v(300, -128.4) * mm, "end": v(300, -129.4) * mm});
            skSolve(sketch);
        }
        {
            var Q0;
            Q0 = qSketchRegion(id + "F137", true);
            extrude(context, id + "F138", {"entities" : qUnion([Q0]), "operationType" : NewBodyOperationType.REMOVE, "oppositeDirection" : true, "depth" : 0.2 * mm});
        }
        {
            var Q0;
            Q0=makeQuery(id+"F122.opExtrude","CAP_FACE",FACE,{"disambiguationData":[OSD([sQuery(id+"F121.wireOp",EDGE,"E124.bottom"),sQuery(id+"F121.wireOp",EDGE,"E124.top"),sQuery(id+"F121.wireOp",EDGE,"E124.left"),sQuery(id+"F121.wireOp",EDGE,"E124.right")])],"isStart":false});
            var sketch = newSketch(context, id + "F139", { "sketchPlane" : qUnion([Q0])});
            skLineSegment(sketch, "E143", {"start": v(250, -148) * mm, "end": v(251, -150) * mm});
            skLineSegment(sketch, "E144", {"start": v(251, -150) * mm, "end": v(250, -150) * mm});
            skLineSegment(sketch, "E145", {"start": v(250, -150) * mm, "end": v(250, -148) * mm});
            skLineSegment(sketch, "E146", {"start": v(258, -148) * mm, "end": v(257, -150) * mm});
            skLineSegment(sketch, "E147", {"start": v(257, -150) * mm, "end": v(258, -150) * mm});
            skLineSegment(sketch, "E148", {"start": v(258, -150) * mm, "end": v(258, -148) * mm});
            skSolve(sketch);
        }
        {
            var Q0;
            Q0 = qSketchRegion(id + "F139", true);
            extrude(context, id + "F140", {"entities" : qUnion([Q0]), "operationType" : NewBodyOperationType.REMOVE, "endBound" : BoundingType.UP_TO_NEXT, "oppositeDirection" : true, "depth" : 25 * mm});
        }
        {
            var Q0;
            Q0=makeQuery(id+"F132.opExtrude","SWEPT_FACE",FACE,{"disambiguationData":[OSD([sQuery(id+"F131.wireOp",EDGE,"E136.bottom")])]});
            var sketch = newSketch(context, id + "F141", { "sketchPlane" : qUnion([Q0])});
            skCircle(sketch, "E149", {"center": v(304, 3) * mm, "radius": 1.25 * mm});
            skPoint(sketch, "E149.centerSnap0", {"position": v(308, 3) * mm});
            skPoint(sketch, "E149.centerSnap1", {"position": v(304, 6) * mm});
            skSolve(sketch);
        }
        {
            var Q0;
            Q0=sQuery(id+"F141.wireOp",EDGE,"E149");
            extrude(context, id + "F142", {"bodyType" : ToolBodyType.SURFACE, "surfaceEntities" : qUnion([Q0]), "depth" : 10 * mm});
        }
        {
            var Q0;
            Q0=makeQuery(id+"F132.opExtrude","CAP_FACE",FACE,{"disambiguationData":[OSD([sQuery(id+"F131.wireOp",EDGE,"E136.bottom"),sQuery(id+"F131.wireOp",EDGE,"E136.top"),sQuery(id+"F131.wireOp",EDGE,"E136.left"),sQuery(id+"F131.wireOp",EDGE,"E136.right")])],"isStart":true});
            var sketch = newSketch(context, id + "F143", { "sketchPlane" : qUnion([Q0])});
            skCircle(sketch, "E150", {"center": v(304, 128.9) * mm, "radius": 1 * mm});
            skPoint(sketch, "E150.centerSnap0", {"position": v(304, 125) * mm});
            skSolve(sketch);
        }
        {
            var Q0;
            Q0 = qSketchRegion(id + "F143", true);
            extrude(context, id + "F144", {"entities" : qUnion([Q0]), "operationType" : NewBodyOperationType.ADD, "depth" : 1.6 * mm});
        }
        {
            var Q0;
            Q0=makeQuery(id+"F132.opExtrude","CAP_FACE",FACE,{"disambiguationData":[OSD([sQuery(id+"F131.wireOp",EDGE,"E136.bottom"),sQuery(id+"F131.wireOp",EDGE,"E136.top"),sQuery(id+"F131.wireOp",EDGE,"E136.left"),sQuery(id+"F131.wireOp",EDGE,"E136.right")])],"isStart":false});
            var sketch = newSketch(context, id + "F145", { "sketchPlane" : qUnion([Q0])});
            skLineSegment(sketch, "E151", {"start": v(300, -148) * mm, "end": v(301, -150) * mm});
            skLineSegment(sketch, "E152", {"start": v(301, -150) * mm, "end": v(300, -150) * mm});
            skLineSegment(sketch, "E153", {"start": v(300, -150) * mm, "end": v(300, -148) * mm});
            skLineSegment(sketch, "E154", {"start": v(308, -148) * mm, "end": v(308, -150) * mm});
            skLineSegment(sketch, "E155", {"start": v(308, -150) * mm, "end": v(307, -150) * mm});
            skLineSegment(sketch, "E156", {"start": v(307, -150) * mm, "end": v(308, -148) * mm});
            skSolve(sketch);
        }
        {
            var Q0;
            Q0 = qSketchRegion(id + "F145", true);
            extrude(context, id + "F146", {"entities" : qUnion([Q0]), "operationType" : NewBodyOperationType.REMOVE, "endBound" : BoundingType.UP_TO_NEXT, "oppositeDirection" : true, "depth" : 25 * mm});
        }
        {
            var Q0;
            Q0=qCreatedBy(makeId("Top.planeOp"),FACE);
            var sketch = newSketch(context, id + "F147", { "sketchPlane" : qUnion([Q0])});
            skLineSegment(sketch, "E157.bottom", {"start": v(46, -183.5) * mm, "end": v(54, -183.5) * mm});
            skLineSegment(sketch, "E157.top", {"start": v(46, -206.5) * mm, "end": v(54, -206.5) * mm});
            skLineSegment(sketch, "E157.left", {"start": v(54, -183.5) * mm, "end": v(54, -206.5) * mm});
            skLineSegment(sketch, "E157.right", {"start": v(46, -183.5) * mm, "end": v(46, -206.5) * mm});
            skLineSegment(sketch, "E158", {"start": v(50, -170.44) * mm, "end": v(50, -221.96) * mm, "construction": true});
            skLineSegment(sketch, "E159", {"start": v(38.13, -200) * mm, "end": v(59.65, -200) * mm, "construction": true});
            skPoint(sketch, "E160", {"position": v(50, -200) * mm});
            skSolve(sketch);
        }
        {
            var Q0;
            Q0 = qSketchRegion(id + "F147", true);
            extrude(context, id + "F148", {"entities" : qUnion([Q0]), "depth" : 5.3 * mm});
        }
        {
            var Q0;
            Q0=makeQuery(id+"F148.opExtrude","CAP_FACE",FACE,{"disambiguationData":[OSD([sQuery(id+"F147.wireOp",EDGE,"E157.bottom"),sQuery(id+"F147.wireOp",EDGE,"E157.top"),sQuery(id+"F147.wireOp",EDGE,"E157.left"),sQuery(id+"F147.wireOp",EDGE,"E157.right")])],"isStart":false});
            var sketch = newSketch(context, id + "F149", { "sketchPlane" : qUnion([Q0])});
            skCircle(sketch, "E161", {"center": v(50, -200) * mm, "radius": 1.55 * mm});
            skSolve(sketch);
        }
        {
            var Q0;
            Q0 = qSketchRegion(id + "F149", true);
            extrude(context, id + "F150", {"entities" : qUnion([Q0]), "operationType" : NewBodyOperationType.REMOVE, "endBound" : BoundingType.UP_TO_NEXT, "oppositeDirection" : true, "depth" : 25 * mm});
        }
        {
            var Q0;
            Q0=makeQuery(id+"F148.opExtrude","CAP_FACE",FACE,{"disambiguationData":[OSD([sQuery(id+"F147.wireOp",EDGE,"E157.bottom"),sQuery(id+"F147.wireOp",EDGE,"E157.top"),sQuery(id+"F147.wireOp",EDGE,"E157.left"),sQuery(id+"F147.wireOp",EDGE,"E157.right")])],"isStart":false});
            var sketch = newSketch(context, id + "F151", { "sketchPlane" : qUnion([Q0])});
            skArc(sketch, "E162", {"start": v(47.94, -184.5) * mm, "mid": v(46.82, -185.32) * mm, "end": v(46, -186.44) * mm});
            skPoint(sketch, "E162.centerSnap0", {"position": v(50, -183.5) * mm});
            skLineSegment(sketch, "E163.bottom", {"start": v(52.06, -184.5) * mm, "end": v(47.94, -184.5) * mm});
            skLineSegment(sketch, "E163.top", {"start": v(52.06, -192.5) * mm, "end": v(47.94, -192.5) * mm});
            skLineSegment(sketch, "E163.left", {"start": v(54, -186.44) * mm, "end": v(54, -190.56) * mm});
            skLineSegment(sketch, "E163.right", {"start": v(46, -186.44) * mm, "end": v(46, -190.56) * mm});
            skPoint(sketch, "E164.orphan", {"position": v(46, -184.5) * mm});
            skPoint(sketch, "E165.orphan", {"position": v(54, -184.5) * mm});
            skArc(sketch, "E166.trimOffspring", {"start": v(54, -186.44) * mm, "mid": v(53.18, -185.32) * mm, "end": v(52.06, -184.5) * mm});
            skArc(sketch, "E167.trimOffspring", {"start": v(46, -190.56) * mm, "mid": v(46.82, -191.68) * mm, "end": v(47.94, -192.5) * mm});
            skArc(sketch, "E168.trimOffspring", {"start": v(52.06, -192.5) * mm, "mid": v(53.18, -191.68) * mm, "end": v(54, -190.56) * mm});
            skPoint(sketch, "E169.orphan", {"position": v(46, -192.5) * mm});
            skPoint(sketch, "E170.orphan", {"position": v(54, -192.5) * mm});
            skSolve(sketch);
        }
        {
            var Q0;
            Q0 = qSketchRegion(id + "F151", true);
            extrude(context, id + "F152", {"entities" : qUnion([Q0]), "operationType" : NewBodyOperationType.ADD, "depth" : 2.1 * mm});
        }
        {
            var Q0;
            Q0=makeQuery(id+"F148.opExtrude","SWEPT_FACE",FACE,{"disambiguationData":[OSD([sQuery(id+"F147.wireOp",EDGE,"E157.top")])]});
            var sketch = newSketch(context, id + "F153", { "sketchPlane" : qUnion([Q0])});
            skLineSegment(sketch, "E171.bottom", {"start": v(46.85, 0) * mm, "end": v(53.15, 0) * mm});
            skLineSegment(sketch, "E171.top", {"start": v(46.85, 5) * mm, "end": v(53.15, 5) * mm});
            skLineSegment(sketch, "E171.left", {"start": v(46.85, 0) * mm, "end": v(46.85, 5) * mm});
            skLineSegment(sketch, "E171.right", {"start": v(53.15, 0) * mm, "end": v(53.15, 5) * mm});
            skLineSegment(sketch, "E172", {"start": v(50, -2.85) * mm, "end": v(50, 11.75) * mm, "construction": true});
            skPoint(sketch, "E172.startSnap0", {"position": v(50, 0) * mm});
            skSolve(sketch);
        }
        {
            var Q0;
            Q0 = qSketchRegion(id + "F153", true);
            extrude(context, id + "F154", {"entities" : qUnion([Q0]), "operationType" : NewBodyOperationType.ADD, "depth" : 1 * mm});
        }
        {
            var Q0;
            Q0=makeQuery(id+"F152.opExtrude","CAP_FACE",FACE,{"disambiguationData":[OSD([sQuery(id+"F151.wireOp",EDGE,"E162"),sQuery(id+"F151.wireOp",EDGE,"E163.bottom"),sQuery(id+"F151.wireOp",EDGE,"E163.top"),sQuery(id+"F151.wireOp",EDGE,"E163.left"),sQuery(id+"F151.wireOp",EDGE,"E163.right"),sQuery(id+"F151.wireOp",EDGE,"E166.trimOffspring"),sQuery(id+"F151.wireOp",EDGE,"E167.trimOffspring"),sQuery(id+"F151.wireOp",EDGE,"E168.trimOffspring")])],"isStart":false});
            var sketch = newSketch(context, id + "F155", { "sketchPlane" : qUnion([Q0])});
            skCircle(sketch, "E173", {"center": v(50, -188.5) * mm, "radius": 0.5 * mm});
            skSolve(sketch);
        }
        {
            var Q0;
            Q0 = qSketchRegion(id + "F155", true);
            extrude(context, id + "F156", {"entities" : qUnion([Q0]), "operationType" : NewBodyOperationType.REMOVE, "oppositeDirection" : true, "depth" : 1 * mm});
        }
        {
            var Q0;
            Q0=makeQuery(id+"F148.opExtrude","SWEPT_EDGE",EDGE,{"disambiguationData":[OSD([sQuery(id+"F147.wireOp",EDGE,"E157.bottom"),sQuery(id+"F147.wireOp",EDGE,"E157.left")])]});
            var Q1;
            Q1=makeQuery(id+"F148.opExtrude","SWEPT_EDGE",EDGE,{"disambiguationData":[OSD([sQuery(id+"F147.wireOp",EDGE,"E157.bottom"),sQuery(id+"F147.wireOp",EDGE,"E157.right")])]});
            chamfer(context, id + "F157", {"entities" : qUnion([Q0, Q1]), "width" : 1.5 * mm, "tangentPropagation" : true});
        }
        {
            var Q0;
            Q0=makeQuery(id+"F154.opExtrude","CAP_FACE",FACE,{"disambiguationData":[OSD([sQuery(id+"F153.wireOp",EDGE,"E171.bottom"),sQuery(id+"F153.wireOp",EDGE,"E171.top"),sQuery(id+"F153.wireOp",EDGE,"E171.left"),sQuery(id+"F153.wireOp",EDGE,"E171.right")])],"isStart":false});
            var sketch = newSketch(context, id + "F158", { "sketchPlane" : qUnion([Q0])});
            skCircle(sketch, "E174", {"center": v(50, 2.5) * mm, "radius": 1.5 * mm});
            skPoint(sketch, "E174.centerSnap0", {"position": v(53.15, 2.5) * mm});
            skPoint(sketch, "E174.centerSnap1", {"position": v(50, 0) * mm});
            skSolve(sketch);
        }
        {
            var Q0;
            Q0 = qSketchRegion(id + "F158", true);
            extrude(context, id + "F159", {"entities" : qUnion([Q0]), "operationType" : NewBodyOperationType.ADD, "depth" : 10 * mm});
        }
        {
            var Q0;
            Q0=makeQuery(id+"F152.opExtrude","CAP_FACE",FACE,{"disambiguationData":[OSD([sQuery(id+"F151.wireOp",EDGE,"E162"),sQuery(id+"F151.wireOp",EDGE,"E163.bottom"),sQuery(id+"F151.wireOp",EDGE,"E163.top"),sQuery(id+"F151.wireOp",EDGE,"E163.left"),sQuery(id+"F151.wireOp",EDGE,"E163.right"),sQuery(id+"F151.wireOp",EDGE,"E166.trimOffspring"),sQuery(id+"F151.wireOp",EDGE,"E167.trimOffspring"),sQuery(id+"F151.wireOp",EDGE,"E168.trimOffspring")])],"isStart":false});
            var sketch = newSketch(context, id + "F160", { "sketchPlane" : qUnion([Q0])});
            skLineSegment(sketch, "E175.bottom", {"start": v(52.5, -188.25) * mm, "end": v(47.5, -188.25) * mm});
            skLineSegment(sketch, "E175.top", {"start": v(52.5, -188.75) * mm, "end": v(47.5, -188.75) * mm});
            skLineSegment(sketch, "E175.left", {"start": v(52.5, -188.25) * mm, "end": v(52.5, -188.75) * mm});
            skLineSegment(sketch, "E175.right", {"start": v(47.5, -188.25) * mm, "end": v(47.5, -188.75) * mm});
            skPoint(sketch, "E175.middle", {"position": v(50, -188.5) * mm});
            skLineSegment(sketch, "E176.bottom", {"start": v(50.21, -186) * mm, "end": v(49.79, -186) * mm});
            skLineSegment(sketch, "E176.top", {"start": v(50.21, -191) * mm, "end": v(49.79, -191) * mm});
            skLineSegment(sketch, "E176.left", {"start": v(50.21, -186) * mm, "end": v(50.21, -191) * mm});
            skLineSegment(sketch, "E176.right", {"start": v(49.79, -186) * mm, "end": v(49.79, -191) * mm});
            skSolve(sketch);
        }
        {
            var Q0;
            Q0 = qSketchRegion(id + "F160", true);
            extrude(context, id + "F161", {"entities" : qUnion([Q0]), "operationType" : NewBodyOperationType.REMOVE, "oppositeDirection" : true, "depth" : 0.5 * mm});
        }
        {
            var Q0;
            Q0=qCreatedBy(makeId("Top.planeOp"),FACE);
            var sketch = newSketch(context, id + "F162", { "sketchPlane" : qUnion([Q0])});
            skLineSegment(sketch, "E177.bottom", {"start": v(96, -206.5) * mm, "end": v(104, -206.5) * mm});
            skLineSegment(sketch, "E177.top", {"start": v(96, -181.5) * mm, "end": v(104, -181.5) * mm});
            skLineSegment(sketch, "E177.left", {"start": v(96, -206.5) * mm, "end": v(96, -181.5) * mm});
            skLineSegment(sketch, "E177.right", {"start": v(104, -206.5) * mm, "end": v(104, -181.5) * mm});
            skLineSegment(sketch, "E178", {"start": v(100, -176.75) * mm, "end": v(100, -206.5) * mm, "construction": true});
            skSolve(sketch);
        }
        {
            var Q0;
            Q0 = qSketchRegion(id + "F162", true);
            extrude(context, id + "F163", {"entities" : qUnion([Q0]), "depth" : 5.3 * mm});
        }
        {
            var Q0;
            Q0=makeQuery(id+"F163.opExtrude","CAP_FACE",FACE,{"disambiguationData":[OSD([sQuery(id+"F162.wireOp",EDGE,"E177.bottom"),sQuery(id+"F162.wireOp",EDGE,"E177.top"),sQuery(id+"F162.wireOp",EDGE,"E177.left"),sQuery(id+"F162.wireOp",EDGE,"E177.right")])],"isStart":false});
            var sketch = newSketch(context, id + "F164", { "sketchPlane" : qUnion([Q0])});
            skCircle(sketch, "E179", {"center": v(100, -200) * mm, "radius": 1.55 * mm});
            skSolve(sketch);
        }
        {
            var Q0;
            Q0 = qSketchRegion(id + "F164", true);
            extrude(context, id + "F165", {"entities" : qUnion([Q0]), "operationType" : NewBodyOperationType.REMOVE, "endBound" : BoundingType.UP_TO_NEXT, "oppositeDirection" : true, "depth" : 25 * mm});
        }
        {
            var Q0;
            Q0=makeQuery(id+"F163.opExtrude","CAP_FACE",FACE,{"disambiguationData":[OSD([sQuery(id+"F162.wireOp",EDGE,"E177.bottom"),sQuery(id+"F162.wireOp",EDGE,"E177.top"),sQuery(id+"F162.wireOp",EDGE,"E177.left"),sQuery(id+"F162.wireOp",EDGE,"E177.right")])],"isStart":false});
            var sketch = newSketch(context, id + "F166", { "sketchPlane" : qUnion([Q0])});
            skLineSegment(sketch, "E180.bottom", {"start": v(96, -181.5) * mm, "end": v(104, -181.5) * mm});
            skLineSegment(sketch, "E180.top", {"start": v(96, -190.3) * mm, "end": v(104, -190.3) * mm});
            skLineSegment(sketch, "E180.left", {"start": v(96, -181.5) * mm, "end": v(96, -190.3) * mm});
            skLineSegment(sketch, "E180.right", {"start": v(104, -181.5) * mm, "end": v(104, -190.3) * mm});
            skSolve(sketch);
        }
        {
            var Q0;
            Q0 = qSketchRegion(id + "F166", true);
            extrude(context, id + "F167", {"entities" : qUnion([Q0]), "operationType" : NewBodyOperationType.ADD, "depth" : 3.8 * mm});
        }
        {
            var Q0;
            Q0=makeQuery(id+"F167.boolean.opBoolean","MERGE",FACE,{"derivedFrom":[makeQuery(id+"F163.opExtrude","SWEPT_FACE",FACE,{"disambiguationData":[OSD([sQuery(id+"F162.wireOp",EDGE,"E177.left")])]}),makeQuery(id+"F167.opExtrude","SWEPT_FACE",FACE,{"disambiguationData":[OSD([sQuery(id+"F166.wireOp",EDGE,"E180.left")])]})]});
            var sketch = newSketch(context, id + "F168", { "sketchPlane" : qUnion([Q0])});
            skLineSegment(sketch, "E181", {"start": v(190.3, 5.3) * mm, "end": v(188.3, 9.1) * mm});
            skLineSegment(sketch, "E182", {"start": v(188.3, 9.1) * mm, "end": v(190.3, 9.1) * mm});
            skLineSegment(sketch, "E183", {"start": v(190.3, 9.1) * mm, "end": v(190.3, 5.3) * mm});
            skSolve(sketch);
        }
        {
            var Q0;
            Q0 = qSketchRegion(id + "F168", true);
            extrude(context, id + "F169", {"entities" : qUnion([Q0]), "operationType" : NewBodyOperationType.REMOVE, "endBound" : BoundingType.UP_TO_NEXT, "oppositeDirection" : true, "depth" : 25 * mm});
        }
        {
            var Q0;
            Q0=makeQuery(id+"F163.opExtrude","SWEPT_FACE",FACE,{"disambiguationData":[OSD([sQuery(id+"F162.wireOp",EDGE,"E177.bottom")])]});
            var sketch = newSketch(context, id + "F170", { "sketchPlane" : qUnion([Q0])});
            skLineSegment(sketch, "E184.bottom", {"start": v(96.85, 0) * mm, "end": v(103.15, 0) * mm});
            skLineSegment(sketch, "E184.top", {"start": v(96.85, 5) * mm, "end": v(103.15, 5) * mm});
            skLineSegment(sketch, "E184.left", {"start": v(96.85, 0) * mm, "end": v(96.85, 5) * mm});
            skLineSegment(sketch, "E184.right", {"start": v(103.15, 0) * mm, "end": v(103.15, 5) * mm});
            skSolve(sketch);
        }
        {
            var Q0;
            Q0 = qSketchRegion(id + "F170", true);
            extrude(context, id + "F171", {"entities" : qUnion([Q0]), "operationType" : NewBodyOperationType.ADD, "depth" : 1 * mm});
        }
        {
            var Q0;
            Q0=makeQuery(id+"F171.opExtrude","CAP_FACE",FACE,{"disambiguationData":[OSD([sQuery(id+"F170.wireOp",EDGE,"E184.bottom"),sQuery(id+"F170.wireOp",EDGE,"E184.top"),sQuery(id+"F170.wireOp",EDGE,"E184.left"),sQuery(id+"F170.wireOp",EDGE,"E184.right")])],"isStart":false});
            var sketch = newSketch(context, id + "F172", { "sketchPlane" : qUnion([Q0])});
            skCircle(sketch, "E185", {"center": v(100, 2.5) * mm, "radius": 1.5 * mm});
            skPoint(sketch, "E185.centerSnap0", {"position": v(103.15, 2.5) * mm});
            skPoint(sketch, "E185.centerSnap1", {"position": v(100, 5) * mm});
            skSolve(sketch);
        }
        {
            var Q0;
            Q0 = qSketchRegion(id + "F172", true);
            extrude(context, id + "F173", {"entities" : qUnion([Q0]), "operationType" : NewBodyOperationType.ADD, "depth" : 10 * mm});
        }
        {
            var Q0;
            Q0=makeQuery(id+"F167.boolean.opBoolean","MERGE",FACE,{"derivedFrom":[makeQuery(id+"F163.opExtrude","SWEPT_FACE",FACE,{"disambiguationData":[OSD([sQuery(id+"F162.wireOp",EDGE,"E177.top")])]}),makeQuery(id+"F167.opExtrude","SWEPT_FACE",FACE,{"disambiguationData":[OSD([sQuery(id+"F166.wireOp",EDGE,"E180.bottom")])]})]});
            var sketch = newSketch(context, id + "F174", { "sketchPlane" : qUnion([Q0])});
            skArc(sketch, "E186", {"start": v(-96, 6.04) * mm, "mid": v(-97, 7.6) * mm, "end": v(-98.56, 8.6) * mm});
            skPoint(sketch, "E186.centerSnap0", {"position": v(-100, 0) * mm});
            skLineSegment(sketch, "E187.bottom", {"start": v(-104, 9.1) * mm, "end": v(-96, 9.1) * mm});
            skLineSegment(sketch, "E187.left", {"start": v(-104, 9.1) * mm, "end": v(-104, 6.04) * mm});
            skLineSegment(sketch, "E187.right", {"start": v(-96, 9.1) * mm, "end": v(-96, 6.04) * mm});
            skLineSegment(sketch, "E188", {"start": v(-101.44, 8.6) * mm, "end": v(-98.56, 8.6) * mm});
            skArc(sketch, "E189.trimOffspring", {"start": v(-101.44, 8.6) * mm, "mid": v(-103, 7.6) * mm, "end": v(-104, 6.04) * mm});
            skPoint(sketch, "E190.orphan", {"position": v(-96, 8.6) * mm});
            skSolve(sketch);
        }
        {
            var Q0;
            Q0 = qSketchRegion(id + "F174", true);
            extrude(context, id + "F175", {"entities" : qUnion([Q0]), "operationType" : NewBodyOperationType.REMOVE, "endBound" : BoundingType.UP_TO_NEXT, "oppositeDirection" : true, "depth" : 25 * mm});
        }
        {
            var Q0;
            Q0=makeQuery(id+"F175.boolean.opBoolean","COPY",FACE,{"derivedFrom":makeQuery(id+"F175.opExtrude","SWEPT_FACE",FACE,{"disambiguationData":[OSD([sQuery(id+"F174.wireOp",EDGE,"E188")])]})});
            var sketch = newSketch(context, id + "F176", { "sketchPlane" : qUnion([Q0])});
            skLineSegment(sketch, "E191.bottom", {"start": v(98.56, -188.56) * mm, "end": v(101.44, -188.56) * mm});
            skLineSegment(sketch, "E191.top", {"start": v(98.56, -185.35) * mm, "end": v(101.44, -185.35) * mm});
            skLineSegment(sketch, "E191.left", {"start": v(98.56, -188.56) * mm, "end": v(98.56, -185.35) * mm});
            skLineSegment(sketch, "E191.right", {"start": v(101.44, -188.56) * mm, "end": v(101.44, -185.35) * mm});
            skSolve(sketch);
        }
        {
            var Q0;
            Q0 = qSketchRegion(id + "F176", true);
            extrude(context, id + "F177", {"entities" : qUnion([Q0]), "operationType" : NewBodyOperationType.ADD, "depth" : 0.5 * mm});
        }
        {
            var Q0;
            Q0=makeQuery(id+"F167.boolean.opBoolean","MERGE",FACE,{"derivedFrom":[makeQuery(id+"F163.opExtrude","SWEPT_FACE",FACE,{"disambiguationData":[OSD([sQuery(id+"F162.wireOp",EDGE,"E177.top")])]}),makeQuery(id+"F167.opExtrude","SWEPT_FACE",FACE,{"disambiguationData":[OSD([sQuery(id+"F166.wireOp",EDGE,"E180.bottom")])]})]});
            var sketch = newSketch(context, id + "F178", { "sketchPlane" : qUnion([Q0])});
            skCircle(sketch, "E192", {"center": v(-100, 4.6) * mm, "radius": 1 * mm});
            skSolve(sketch);
        }
        {
            var Q0;
            Q0 = qSketchRegion(id + "F178", true);
            extrude(context, id + "F179", {"entities" : qUnion([Q0]), "operationType" : NewBodyOperationType.REMOVE, "oppositeDirection" : true, "depth" : 1 * mm});
        }
        {
            var Q0;
            Q0=makeQuery(id+"F167.boolean.opBoolean","MERGE",FACE,{"derivedFrom":[makeQuery(id+"F163.opExtrude","SWEPT_FACE",FACE,{"disambiguationData":[OSD([sQuery(id+"F162.wireOp",EDGE,"E177.top")])]}),makeQuery(id+"F167.opExtrude","SWEPT_FACE",FACE,{"disambiguationData":[OSD([sQuery(id+"F166.wireOp",EDGE,"E180.bottom")])]})]});
            var sketch = newSketch(context, id + "F180", { "sketchPlane" : qUnion([Q0])});
            skLineSegment(sketch, "E193.bottom", {"start": v(-97, 4.85) * mm, "end": v(-103, 4.85) * mm});
            skLineSegment(sketch, "E193.top", {"start": v(-97, 4.35) * mm, "end": v(-103, 4.35) * mm});
            skLineSegment(sketch, "E193.left", {"start": v(-97, 4.85) * mm, "end": v(-97, 4.35) * mm});
            skLineSegment(sketch, "E193.right", {"start": v(-103, 4.85) * mm, "end": v(-103, 4.35) * mm});
            skPoint(sketch, "E193.middle", {"position": v(-100, 4.6) * mm});
            skLineSegment(sketch, "E194.bottom", {"start": v(-99.75, 7.6) * mm, "end": v(-100.25, 7.6) * mm});
            skLineSegment(sketch, "E194.top", {"start": v(-99.75, 1.6) * mm, "end": v(-100.25, 1.6) * mm});
            skLineSegment(sketch, "E194.left", {"start": v(-99.75, 7.6) * mm, "end": v(-99.75, 1.6) * mm});
            skLineSegment(sketch, "E194.right", {"start": v(-100.25, 7.6) * mm, "end": v(-100.25, 1.6) * mm});
            skSolve(sketch);
        }
        {
            var Q0;
            Q0 = qSketchRegion(id + "F180", true);
            extrude(context, id + "F181", {"entities" : qUnion([Q0]), "operationType" : NewBodyOperationType.REMOVE, "oppositeDirection" : true, "depth" : 0.5 * mm});
        }
        {
            var Q0;
            Q0=makeQuery(id+"F167.boolean.opBoolean","MERGE",FACE,{"derivedFrom":[makeQuery(id+"F163.opExtrude","SWEPT_FACE",FACE,{"disambiguationData":[OSD([sQuery(id+"F162.wireOp",EDGE,"E177.top")])]}),makeQuery(id+"F167.opExtrude","SWEPT_FACE",FACE,{"disambiguationData":[OSD([sQuery(id+"F166.wireOp",EDGE,"E180.bottom")])]})]});
            var sketch = newSketch(context, id + "F182", { "sketchPlane" : qUnion([Q0])});
            skLineSegment(sketch, "E195.bottom", {"start": v(-104, 0) * mm, "end": v(-96, 0) * mm});
            skLineSegment(sketch, "E195.top", {"start": v(-104, 0.4) * mm, "end": v(-96, 0.4) * mm});
            skLineSegment(sketch, "E195.left", {"start": v(-104, 0) * mm, "end": v(-104, 0.4) * mm});
            skLineSegment(sketch, "E195.right", {"start": v(-96, 0) * mm, "end": v(-96, 0.4) * mm});
            skSolve(sketch);
        }
        {
            var Q0;
            Q0 = qSketchRegion(id + "F182", true);
            extrude(context, id + "F183", {"entities" : qUnion([Q0]), "operationType" : NewBodyOperationType.REMOVE, "oppositeDirection" : true, "depth" : 2.5 * mm});
        }
        {
            var Q0;
            Q0=qCreatedBy(makeId("Top.planeOp"),FACE);
            var sketch = newSketch(context, id + "F184", { "sketchPlane" : qUnion([Q0])});
            skLineSegment(sketch, "E196.bottom", {"start": v(50, -300) * mm, "end": v(54, -300) * mm});
            skLineSegment(sketch, "E196.top", {"start": v(50, -278) * mm, "end": v(54, -278) * mm});
            skLineSegment(sketch, "E196.left", {"start": v(50, -300) * mm, "end": v(50, -278) * mm});
            skLineSegment(sketch, "E196.right", {"start": v(54, -300) * mm, "end": v(54, -278) * mm});
            skSolve(sketch);
        }
        {
            var Q0;
            Q0 = qSketchRegion(id + "F184", true);
            extrude(context, id + "F185", {"entities" : qUnion([Q0]), "depth" : 4 * mm});
        }
        {
            var Q0;
            Q0=makeQuery(id+"F185.opExtrude","SWEPT_FACE",FACE,{"disambiguationData":[OSD([sQuery(id+"F184.wireOp",EDGE,"E196.bottom")])]});
            var sketch = newSketch(context, id + "F186", { "sketchPlane" : qUnion([Q0])});
            skCircle(sketch, "E197", {"center": v(52, 2) * mm, "radius": 1.4 * mm});
            skPoint(sketch, "E197.centerSnap0", {"position": v(50, 2) * mm});
            skPoint(sketch, "E197.centerSnap1", {"position": v(52, 4) * mm});
            skSolve(sketch);
        }
        {
            var Q0;
            Q0 = qSketchRegion(id + "F186", true);
            extrude(context, id + "F187", {"entities" : qUnion([Q0]), "operationType" : NewBodyOperationType.ADD, "depth" : 10 * mm});
        }
        {
            var Q0;
            Q0=makeQuery(id+"F185.opExtrude","CAP_FACE",FACE,{"disambiguationData":[OSD([sQuery(id+"F184.wireOp",EDGE,"E196.bottom"),sQuery(id+"F184.wireOp",EDGE,"E196.top"),sQuery(id+"F184.wireOp",EDGE,"E196.left"),sQuery(id+"F184.wireOp",EDGE,"E196.right")])],"isStart":false});
            var sketch = newSketch(context, id + "F188", { "sketchPlane" : qUnion([Q0])});
            skCircle(sketch, "E198", {"center": v(52, -280) * mm, "radius": 1.5 * mm});
            skPoint(sketch, "E198.centerSnap0", {"position": v(52, -278) * mm});
            skSolve(sketch);
        }
        {
            var Q0;
            Q0=makeQuery(id+"F188.imprint","IMPRINT",FACE,{"disambiguationData":[TD([[makeQuery(id+"F188.imprint","IMPRINT",EDGE,{"derivedFrom":sQuery(id+"F188.wireOp",EDGE,"E198")}),1.0]])]});
            var Q1;
            Q1=sQuery(id+"F188.wireOp",EDGE,"E198");
            extrude(context, id + "F189", {"entities" : qUnion([Q0]), "operationType" : NewBodyOperationType.REMOVE, "surfaceEntities" : qUnion([Q1]), "oppositeDirection" : true, "depth" : 0.2 * mm});
        }
        {
            var Q0;
            Q0=qCreatedBy(makeId("Top.planeOp"),FACE);
            var sketch = newSketch(context, id + "F190", { "sketchPlane" : qUnion([Q0])});
            skLineSegment(sketch, "E199.bottom", {"start": v(100, -300) * mm, "end": v(106, -300) * mm});
            skLineSegment(sketch, "E199.top", {"start": v(100, -280) * mm, "end": v(106, -280) * mm});
            skLineSegment(sketch, "E199.left", {"start": v(100, -300) * mm, "end": v(100, -280) * mm});
            skLineSegment(sketch, "E199.right", {"start": v(106, -300) * mm, "end": v(106, -280) * mm});
            skSolve(sketch);
        }
        {
            var Q0;
            Q0 = qSketchRegion(id + "F190", true);
            extrude(context, id + "F191", {"entities" : qUnion([Q0]), "depth" : 6 * mm});
        }
        {
            var Q0;
            Q0=makeQuery(id+"F191.opExtrude","SWEPT_FACE",FACE,{"disambiguationData":[OSD([sQuery(id+"F190.wireOp",EDGE,"E199.bottom")])]});
            var sketch = newSketch(context, id + "F192", { "sketchPlane" : qUnion([Q0])});
            skCircle(sketch, "E200", {"center": v(103, 3) * mm, "radius": 1.4 * mm});
            skPoint(sketch, "E200.centerSnap0", {"position": v(106, 3) * mm});
            skPoint(sketch, "E200.centerSnap1", {"position": v(103, 6) * mm});
            skSolve(sketch);
        }
        {
            var Q0;
            Q0 = qSketchRegion(id + "F192", true);
            extrude(context, id + "F193", {"entities" : qUnion([Q0]), "operationType" : NewBodyOperationType.ADD, "depth" : 10 * mm});
        }
        {
            var Q0;
            Q0=makeQuery(id+"F191.opExtrude","CAP_FACE",FACE,{"disambiguationData":[OSD([sQuery(id+"F190.wireOp",EDGE,"E199.bottom"),sQuery(id+"F190.wireOp",EDGE,"E199.top"),sQuery(id+"F190.wireOp",EDGE,"E199.left"),sQuery(id+"F190.wireOp",EDGE,"E199.right")])],"isStart":false});
            var sketch = newSketch(context, id + "F194", { "sketchPlane" : qUnion([Q0])});
            skCircle(sketch, "E201", {"center": v(103, -283) * mm, "radius": 2 * mm});
            skPoint(sketch, "E201.centerSnap0", {"position": v(103, -280) * mm});
            skSolve(sketch);
        }
        {
            var Q0;
            Q0 = qSketchRegion(id + "F194", true);
            extrude(context, id + "F195", {"entities" : qUnion([Q0]), "operationType" : NewBodyOperationType.REMOVE, "oppositeDirection" : true, "depth" : 0.2 * mm});
        }
        {
            var Q0;
            Q0=qCreatedBy(makeId("Top.planeOp"),FACE);
            var sketch = newSketch(context, id + "F196", { "sketchPlane" : qUnion([Q0])});
            skLineSegment(sketch, "E202.bottom", {"start": v(150, -300) * mm, "end": v(156, -300) * mm});
            skLineSegment(sketch, "E202.top", {"start": v(150, -270) * mm, "end": v(156, -270) * mm});
            skLineSegment(sketch, "E202.left", {"start": v(150, -300) * mm, "end": v(150, -270) * mm});
            skLineSegment(sketch, "E202.right", {"start": v(156, -300) * mm, "end": v(156, -270) * mm});
            skSolve(sketch);
        }
        {
            var Q0;
            Q0 = qSketchRegion(id + "F196", true);
            extrude(context, id + "F197", {"entities" : qUnion([Q0]), "depth" : 6 * mm});
        }
        {
            var Q0;
            Q0=makeQuery(id+"F197.opExtrude","SWEPT_FACE",FACE,{"disambiguationData":[OSD([sQuery(id+"F196.wireOp",EDGE,"E202.bottom")])]});
            var sketch = newSketch(context, id + "F198", { "sketchPlane" : qUnion([Q0])});
            skCircle(sketch, "E203", {"center": v(153, 3) * mm, "radius": 1.4 * mm});
            skPoint(sketch, "E203.centerSnap0", {"position": v(150, 3) * mm});
            skPoint(sketch, "E203.centerSnap1", {"position": v(153, 6) * mm});
            skSolve(sketch);
        }
        {
            var Q0;
            Q0 = qSketchRegion(id + "F198", true);
            extrude(context, id + "F199", {"entities" : qUnion([Q0]), "operationType" : NewBodyOperationType.ADD, "depth" : 10 * mm});
        }
        {
            var Q0;
            Q0=makeQuery(id+"F197.opExtrude","CAP_FACE",FACE,{"disambiguationData":[OSD([sQuery(id+"F196.wireOp",EDGE,"E202.bottom"),sQuery(id+"F196.wireOp",EDGE,"E202.top"),sQuery(id+"F196.wireOp",EDGE,"E202.left"),sQuery(id+"F196.wireOp",EDGE,"E202.right")])],"isStart":false});
            var sketch = newSketch(context, id + "F200", { "sketchPlane" : qUnion([Q0])});
            skCircle(sketch, "E204", {"center": v(153, -274) * mm, "radius": 2 * mm});
            skPoint(sketch, "E204.centerSnap0", {"position": v(153, -270) * mm});
            skSolve(sketch);
        }
        {
            var Q0;
            Q0 = qSketchRegion(id + "F200", true);
            extrude(context, id + "F201", {"entities" : qUnion([Q0]), "operationType" : NewBodyOperationType.REMOVE, "oppositeDirection" : true, "depth" : 0.2 * mm});
        }
        {
            var Q0;
            Q0=qCreatedBy(makeId("Top.planeOp"),FACE);
            var sketch = newSketch(context, id + "F202", { "sketchPlane" : qUnion([Q0])});
            skLineSegment(sketch, "E205.bottom", {"start": v(200, -300) * mm, "end": v(208, -300) * mm});
            skLineSegment(sketch, "E205.top", {"start": v(200, -284) * mm, "end": v(208, -284) * mm});
            skLineSegment(sketch, "E205.left", {"start": v(200, -300) * mm, "end": v(200, -284) * mm});
            skLineSegment(sketch, "E205.right", {"start": v(208, -300) * mm, "end": v(208, -284) * mm});
            skSolve(sketch);
        }
        {
            var Q0;
            Q0 = qSketchRegion(id + "F202", true);
            extrude(context, id + "F203", {"entities" : qUnion([Q0]), "depth" : 4.7 * mm});
        }
        {
            var Q0;
            Q0=makeQuery(id+"F203.opExtrude","CAP_FACE",FACE,{"disambiguationData":[OSD([sQuery(id+"F202.wireOp",EDGE,"E205.bottom"),sQuery(id+"F202.wireOp",EDGE,"E205.top"),sQuery(id+"F202.wireOp",EDGE,"E205.left"),sQuery(id+"F202.wireOp",EDGE,"E205.right")])],"isStart":false});
            var sketch = newSketch(context, id + "F204", { "sketchPlane" : qUnion([Q0])});
            skCircle(sketch, "E206", {"center": v(204, -288) * mm, "radius": 3 * mm});
            skPoint(sketch, "E206.centerSnap0", {"position": v(204, -284) * mm});
            skSolve(sketch);
        }
        {
            var Q0;
            Q0 = qSketchRegion(id + "F204", true);
            extrude(context, id + "F205", {"entities" : qUnion([Q0]), "operationType" : NewBodyOperationType.REMOVE, "oppositeDirection" : true, "depth" : 0.2 * mm});
        }
        {
            var Q0;
            Q0=makeQuery(id+"F203.opExtrude","CAP_FACE",FACE,{"disambiguationData":[OSD([sQuery(id+"F202.wireOp",EDGE,"E205.bottom"),sQuery(id+"F202.wireOp",EDGE,"E205.top"),sQuery(id+"F202.wireOp",EDGE,"E205.left"),sQuery(id+"F202.wireOp",EDGE,"E205.right")])],"isStart":false});
            var sketch = newSketch(context, id + "F206", { "sketchPlane" : qUnion([Q0])});
            skPoint(sketch, "E207", {"position": v(204, -296) * mm});
            skPoint(sketch, "E207.positionSnap0", {"position": v(204, -284) * mm});
            skSolve(sketch);
        }
        {
            var Q0;
            Q0=sQuery(id+"F206.wireOp",VERTEX,"E207");
            var Q1;
            Q1=makeQuery(id+"F203.opExtrude","SWEPT_BODY",BODY,{"disambiguationData":[OSD([sQuery(id+"F202.wireOp",EDGE,"E205.bottom"),sQuery(id+"F202.wireOp",EDGE,"E205.top"),sQuery(id+"F202.wireOp",EDGE,"E205.left"),sQuery(id+"F202.wireOp",EDGE,"E205.right")])]});
            hole(context, id + "F207", {"style" : HoleStyle.C_SINK, "endStyle" : HoleEndStyle.THROUGH, "holeDiameter" : 3.1 * mm, "cSinkDiameter" : 6.5 * mm, "cSinkAngle" : 90 * degree, "startFromSketch" : true, "locations" : qUnion([Q0]), "scope" : qUnion([Q1]), "isTappedThrough" : true});
        }
        {
            var Q0;
            Q0=makeQuery(id+"F203.opExtrude","SWEPT_FACE",FACE,{"disambiguationData":[OSD([sQuery(id+"F202.wireOp",EDGE,"E205.bottom")])]});
            var sketch = newSketch(context, id + "F208", { "sketchPlane" : qUnion([Q0])});
            skLineSegment(sketch, "E208.bottom", {"start": v(207, 0.2) * mm, "end": v(201, 0.2) * mm});
            skLineSegment(sketch, "E208.top", {"start": v(207, 4.5) * mm, "end": v(201, 4.5) * mm});
            skLineSegment(sketch, "E208.left", {"start": v(207, 0.2) * mm, "end": v(207, 4.5) * mm});
            skLineSegment(sketch, "E208.right", {"start": v(201, 0.2) * mm, "end": v(201, 4.5) * mm});
            skPoint(sketch, "E208.middle", {"position": v(204, 2.35) * mm});
            skPoint(sketch, "E208.middle.positionSnap0", {"position": v(204, 4.7) * mm});
            skPoint(sketch, "E208.middle.positionSnap1", {"position": v(208, 2.35) * mm});
            skPoint(sketch, "E208.centerSnap0", {"position": v(204, 4.7) * mm});
            skPoint(sketch, "E208.centerSnap1", {"position": v(208, 2.35) * mm});
            skSolve(sketch);
        }
        {
            var Q0;
            Q0=makeQuery(id+"F208.imprint","IMPRINT",FACE,{"disambiguationData":[TD([[makeQuery(id+"F208.imprint","IMPRINT",EDGE,{"derivedFrom":sQuery(id+"F208.wireOp",EDGE,"E208.bottom")}),-1.0]])]});
            extrude(context, id + "F209", {"entities" : qUnion([Q0]), "operationType" : NewBodyOperationType.ADD, "depth" : 1 * mm});
        }
        {
            var Q0;
            Q0=makeQuery(id+"F209.opExtrude","CAP_FACE",FACE,{"disambiguationData":[OSD([sQuery(id+"F208.wireOp",EDGE,"E208.bottom"),sQuery(id+"F208.wireOp",EDGE,"E208.top"),sQuery(id+"F208.wireOp",EDGE,"E208.left"),sQuery(id+"F208.wireOp",EDGE,"E208.right")])],"isStart":false});
            var sketch = newSketch(context, id + "F210", { "sketchPlane" : qUnion([Q0])});
            skCircle(sketch, "E209", {"center": v(204, 2.35) * mm, "radius": 1.4 * mm});
            skPoint(sketch, "E209.centerSnap0", {"position": v(207, 2.35) * mm});
            skPoint(sketch, "E209.centerSnap1", {"position": v(204, 4.5) * mm});
            skSolve(sketch);
        }
        {
            var Q0;
            Q0 = qSketchRegion(id + "F210", true);
            extrude(context, id + "F211", {"entities" : qUnion([Q0]), "operationType" : NewBodyOperationType.ADD, "depth" : 10 * mm});
        }
        {
            var Q0;
            Q0=makeQuery(id+"F203.opExtrude","SWEPT_EDGE",EDGE,{"disambiguationData":[OSD([sQuery(id+"F202.wireOp",EDGE,"E205.top"),sQuery(id+"F202.wireOp",EDGE,"E205.right")])]});
            var Q1;
            Q1=makeQuery(id+"F203.opExtrude","SWEPT_EDGE",EDGE,{"disambiguationData":[OSD([sQuery(id+"F202.wireOp",EDGE,"E205.bottom"),sQuery(id+"F202.wireOp",EDGE,"E205.right")])]});
            var Q2;
            Q2=makeQuery(id+"F203.opExtrude","SWEPT_EDGE",EDGE,{"disambiguationData":[OSD([sQuery(id+"F202.wireOp",EDGE,"E205.bottom"),sQuery(id+"F202.wireOp",EDGE,"E205.left")])]});
            var Q3;
            Q3=makeQuery(id+"F203.opExtrude","SWEPT_EDGE",EDGE,{"disambiguationData":[OSD([sQuery(id+"F202.wireOp",EDGE,"E205.top"),sQuery(id+"F202.wireOp",EDGE,"E205.left")])]});
            chamfer(context, id + "F212", {"entities" : qUnion([Q0, Q1, Q2, Q3]), "width" : 0.5 * mm, "tangentPropagation" : true});
        }
    });
